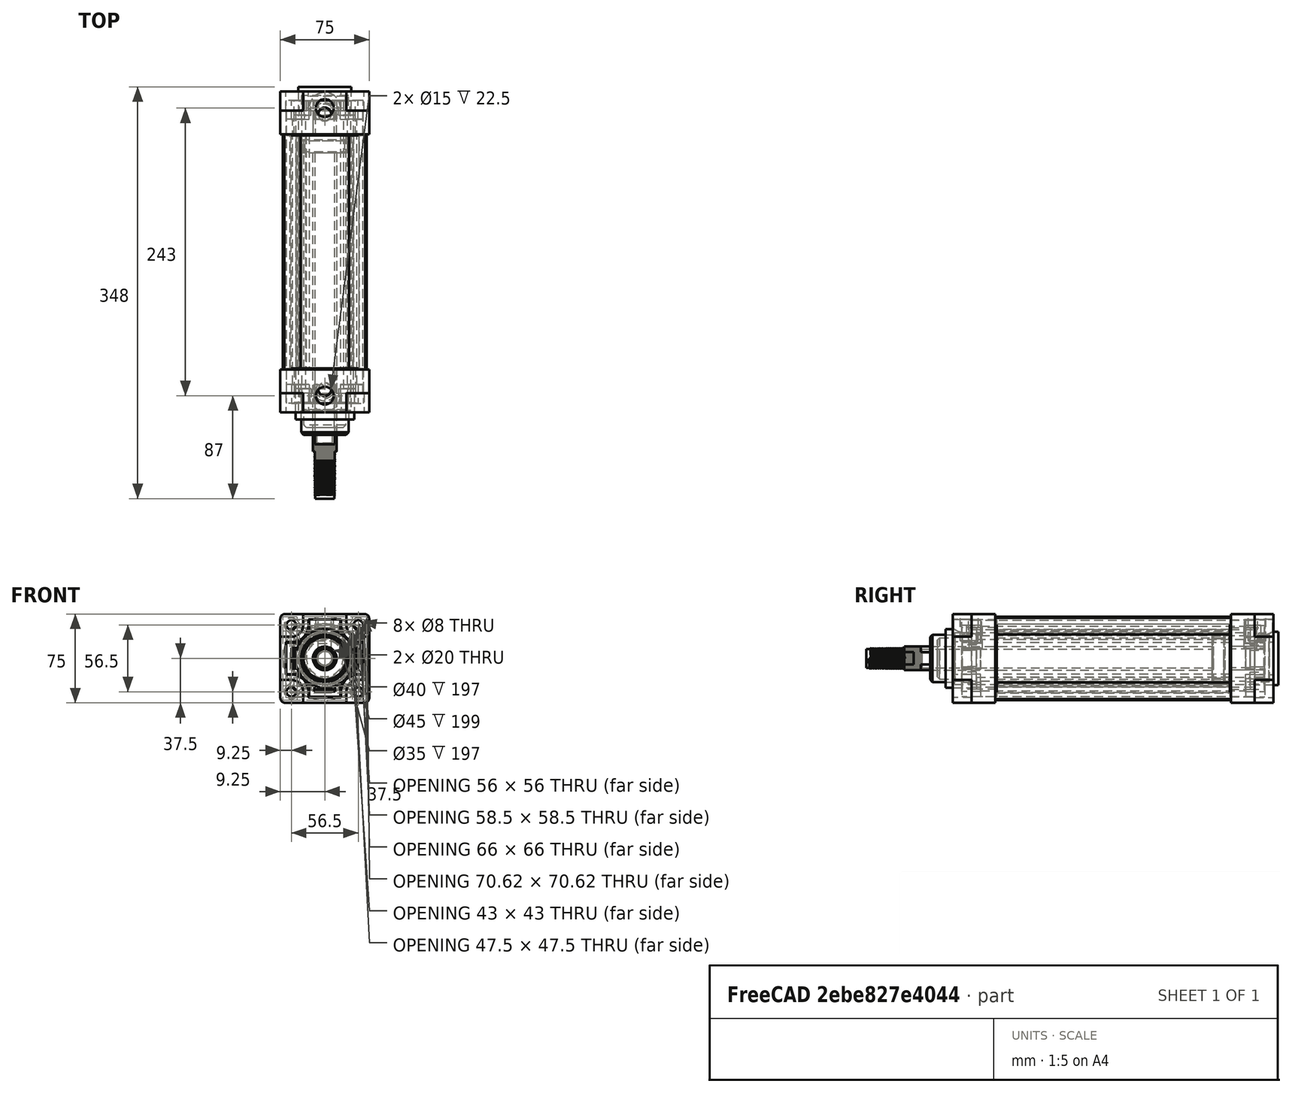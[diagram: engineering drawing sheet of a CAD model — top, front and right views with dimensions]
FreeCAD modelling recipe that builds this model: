
FCSTD DOCUMENT  (FreeCAD 0.18.4R)
Label: DA-XX-XXX-TCA show
Comment: Alejandro Alvarez\nBERSERK.DESIGN\nLicense Design Libre\n
License: Other
LicenseURL: ttps://designlibre.org/license-en/
objects: Sketcher::SketchObject×39, PartDesign::Pad×30, PartDesign::Body×9, PartDesign::Mirrored×6, PartDesign::Pocket×6, Spreadsheet::Sheet×3, PartDesign::Fillet×3, PartDesign::Chamfer×3, Part::Helix×3, PartDesign::ShapeBinder×3, PartDesign::AdditivePipe×3, Part::Fuse×3, App::Part×3, App::MeasureDistance×2
note: 147 computed .brp shape members not serialized (recipe doc carries the construction recipe); baked Part::Feature solids carry a one-line shape summary decoded from their .brp

FEATURE [Spreadsheet::Sheet] Spreadsheet  label="Medidas"
  cells = A1=Medidas Tabla; A2=CARRERRA001; B2(carrera)=150; C2=Delta Carrera; D2(delta)=5; A3=Ø; B3(diametro)=40; A4=AM; B4(am)=24; A5=B; B5(b)=35; A6=BG; B6(bg)=12; A7=EE; B7(ee)=52; A8=EEE; B8(eee)=11; C8=1/4 NPT; A9=GG; B9(gg)=29; A10=KK; B10(kk)=12; C10(kkp)=1.25; A11=KV; B11(kv)=19; A12=KW; B12(kw)=7; A13=L2; B13(l2)=21; A14=L8; B14(l8)=105; A15=MMM; B15(mmm)=16; A16=PL; B16(pl)=11.5; A17=RT; B17(rt)=6; A18=SW; B18(sw)=13; A19=TG; B19(tg)=38; A20=VA; B20(va)=4; A21=VD; B21(vd)=6; A22=VF; B22(vf)=12; A23=VG; B23(vg)=54; A24=WH; B24(wh)=30; A25=XD; B25(xd)=160; A26=AH; B26(ah)=36; A27=SA; B27(sa)=161; A28=XA; B28(xa)=163; A29=Peso Carrera 0; B29=730; A30=(gr.) Cada 10mm; B30=32; A31=Peso Total; B31==B29 + B2 / 10 * B30
FEATURE [Sketcher::SketchObject] Sketch
  MapMode = 5
  Placement = pos=(0,0,0) rot=(1,0,0;1.5708rad)
  Support = -> [XZ_Plane001]
  expr: Constraints[76] = Medidas.rt / 2 * 1.5
  expr: Constraints[72] = Medidas.tg
  expr: Constraints[74] = Medidas.tg * 0.625
  expr: Constraints[75] = Medidas.b / 2
  expr: Constraints[73] = Medidas.rt / 2
  sketch-geometry (29):
    g0: LineSegment [constr] StartX=-19 StartY=19 StartZ=0 EndX=19 EndY=19 EndZ=0
    g1: LineSegment [constr] StartX=19 StartY=19 StartZ=0 EndX=19 EndY=-19 EndZ=0
    g2: LineSegment [constr] StartX=19 StartY=-19 StartZ=0 EndX=-19 EndY=-19 EndZ=0
    g3: LineSegment [constr] StartX=-19 StartY=-19 StartZ=0 EndX=-19 EndY=19 EndZ=0
    g4: LineSegment [constr] StartX=-19 StartY=19 StartZ=0 EndX=0 EndY=0 EndZ=0
    g5: LineSegment [constr] StartX=0 StartY=0 StartZ=0 EndX=19 EndY=-19 EndZ=0
    g6: LineSegment StartX=22.182 StartY=15.818 StartZ=0 EndX=19.6716 EndY=13.3076 EndZ=0
    g7: LineSegment StartX=13.3076 StartY=19.6716 StartZ=0 EndX=15.818 EndY=22.182 EndZ=0
    g8: LineSegment [constr] StartX=0 StartY=0 StartZ=0 EndX=23.75 EndY=0 EndZ=0
    g9: ArcOfCircle CenterX=19 CenterY=19 CenterZ=0 NormalX=0 NormalY=0 NormalZ=1 AngleXU=0 Radius=4.5 StartAngle=5.49779 EndAngle=8.63938
    g10: ArcOfCircle CenterX=0 CenterY=0 CenterZ=0 NormalX=0 NormalY=0 NormalZ=1 AngleXU=0 Radius=23.75 StartAngle=0.976024 EndAngle=2.16557
    g11: LineSegment StartX=22.182 StartY=-15.818 StartZ=0 EndX=19.6716 EndY=-13.3076 EndZ=0
    g12: ArcOfCircle CenterX=19 CenterY=-19 CenterZ=0 NormalX=0 NormalY=0 NormalZ=1 AngleXU=0 Radius=4.5 StartAngle=3.92699 EndAngle=7.06858
    g13: LineSegment StartX=13.3076 StartY=-19.6716 StartZ=0 EndX=15.818 EndY=-22.182 EndZ=0
    g14: LineSegment [constr] StartX=0 StartY=0 StartZ=0 EndX=0 EndY=23.75 EndZ=0
    g15: LineSegment StartX=-22.182 StartY=15.818 StartZ=0 EndX=-19.6716 EndY=13.3076 EndZ=0
    g16: ArcOfCircle CenterX=-19 CenterY=19 CenterZ=0 NormalX=0 NormalY=0 NormalZ=1 AngleXU=0 Radius=4.5 StartAngle=0.785398 EndAngle=3.92699
    g17: LineSegment StartX=-13.3076 StartY=19.6716 StartZ=0 EndX=-15.818 EndY=22.182 EndZ=0
    g18: LineSegment StartX=-22.182 StartY=-15.818 StartZ=0 EndX=-19.6716 EndY=-13.3076 EndZ=0
    g19: ArcOfCircle CenterX=-19 CenterY=-19 CenterZ=0 NormalX=0 NormalY=0 NormalZ=1 AngleXU=0 Radius=4.5 StartAngle=2.35619 EndAngle=5.49779
    g20: LineSegment StartX=-13.3076 StartY=-19.6716 StartZ=0 EndX=-15.818 EndY=-22.182 EndZ=0
    g21: ArcOfCircle CenterX=0 CenterY=0 CenterZ=0 NormalX=0 NormalY=0 NormalZ=1 AngleXU=0 Radius=23.75 StartAngle=2.54682 EndAngle=3.73636
    g22: ArcOfCircle CenterX=0 CenterY=0 CenterZ=0 NormalX=0 NormalY=0 NormalZ=1 AngleXU=0 Radius=23.75 StartAngle=4.11762 EndAngle=5.30716
    g23: ArcOfCircle CenterX=0 CenterY=0 CenterZ=0 NormalX=0 NormalY=0 NormalZ=1 AngleXU=0 Radius=23.75 StartAngle=5.68841 EndAngle=6.87796
    g24: Circle CenterX=0 CenterY=0 CenterZ=0 NormalX=0 NormalY=0 NormalZ=1 AngleXU=0 Radius=17.5
    g25: Circle CenterX=19 CenterY=19 CenterZ=0 NormalX=0 NormalY=0 NormalZ=1 AngleXU=0 Radius=3
    g26: Circle CenterX=-19 CenterY=19 CenterZ=0 NormalX=0 NormalY=0 NormalZ=1 AngleXU=0 Radius=3
    g27: Circle CenterX=-19 CenterY=-19 CenterZ=0 NormalX=0 NormalY=0 NormalZ=1 AngleXU=0 Radius=3
    g28: Circle CenterX=19 CenterY=-19 CenterZ=0 NormalX=0 NormalY=0 NormalZ=1 AngleXU=0 Radius=3
  constraints (78):
    c: Coincident(g0,g1)
    c: Coincident(g1,g2)
    c: Coincident(g2,g3)
    c: Coincident(g3,g0)
    c: Horizontal(g0)
    c: Horizontal(g2)
    c: Vertical(g1)
    c: Vertical(g3)
    c: Coincident(g0,g4)
    c: Coincident(g4,g-1)
    c: Coincident(g4,g5)
    c: Coincident(g5,g1)
    c: Equal(g5,g4)
    c: Parallel(g5,g4)
    c: Equal(g3,g0)
    c: Parallel(g6,g7)
    c: Coincident(g-1,g8)
    c: Horizontal(g8)
    c: Angle(g8,g6) = 0.785398
    c: Coincident(g9,g0)
    c: Coincident(g9,g6)
    c: Coincident(g10,g-1)
    c: Parallel(g11,g13)
    c: Tangent(g12,g13) = -1.5708
    c: Tangent(g12,g11) = -1.5708
    c: PointOnObject(g11,g10)
    c: PointOnObject(g13,g10)
    c: Perpendicular(g6,g11)
    c: Coincident(g12,g1)
    c: Equal(g11,g6)
    c: Tangent(g9,g7) = 1.5708
    c: Equal(g9,g12)
    c: Coincident(g-1,g14)
    c: Vertical(g14)
    c: PointOnObject(g14,g10)
    c: Parallel(g15,g17)
    c: Parallel(g18,g20)
    c: Tangent(g19,g20) = 1.5708
    c: Tangent(g19,g18) = 1.5708
    c: Perpendicular(g15,g18)
    c: Equal(g18,g15)
    c: Tangent(g16,g17) = -1.5708
    c: Equal(g16,g19)
    c: Perpendicular(g7,g17)
    c: Equal(g12,g19)
    c: Coincident(g19,g2)
    c: Coincident(g0,g16)
    c: PointOnObject(g20,g10)
    c: Tangent(g16,g15) = -1.5708
    c: PointOnObject(g15,g10)
    c: Coincident(g10,g7)
    c: Coincident(g23,g6)
    c: Equal(g10,g21)
    c: Coincident(g10,g17)
    c: Coincident(g10,g21)
    c: Equal(g21,g22)
    c: PointOnObject(g21,g18)
    c: PointOnObject(g22,g20)
    c: Coincident(g21,g22)
    c: Equal(g22,g23)
    c: PointOnObject(g23,g11)
    c: Coincident(g22,g23)
    c: PointOnObject(g22,g13)
    c: PointOnObject(g21,g15)
    c: Coincident(g24,g-1)
    c: Coincident(g25,g0)
    c: Coincident(g26,g0)
    c: Coincident(g27,g2)
    c: Coincident(g28,g1)
    c: Equal(g28,g25)
    c: Equal(g25,g26)
    c: Equal(g26,g27)
    c: DistanceX(g0,g0) = 38
    c: Radius(g28) = 3
    c: Radius(g23) = 23.75
    c: Radius(g24) = 17.5
    c: Radius(g12) = 4.5
    c: PointOnObject(g8,g23)
FEATURE [PartDesign::Pad] Pad
  Length = 197
  Length2 = 100
  Midplane = true
  Placement = pos=(0,0,0) rot=(1,0,0;1.5708rad)
  Profile = -> Sketch
  Refine = true
  Type = 0
  expr: Length = Medidas.l8 + Medidas.carrera - 2 * Medidas.gg
FEATURE [Sketcher::SketchObject] Sketch001
  ExternalGeometry = -> [Pad]
  MapMode = 5
  Placement = pos=(0,-98.5,-1.01921e-11) rot=(1,0,0;1.5708rad)
  Support = -> [Pad]
  expr: Constraints[37] = Medidas.mmm / 2
  expr: Constraints[15] = Medidas.ee
  expr: Constraints[33] = Medidas.tg
  expr: Constraints[32] = Medidas.rt / 2
  sketch-geometry (15):
    g0: LineSegment StartX=-26 StartY=26 StartZ=0 EndX=26 EndY=26 EndZ=0
    g1: LineSegment StartX=26 StartY=26 StartZ=0 EndX=26 EndY=-26 EndZ=0
    g2: LineSegment StartX=26 StartY=-26 StartZ=0 EndX=-26 EndY=-26 EndZ=0
    g3: LineSegment StartX=-26 StartY=-26 StartZ=0 EndX=-26 EndY=26 EndZ=0
    g4: LineSegment [constr] StartX=-26 StartY=26 StartZ=0 EndX=0 EndY=0 EndZ=0
    g5: LineSegment [constr] StartX=0 StartY=0 StartZ=0 EndX=26 EndY=-26 EndZ=0
    g6: Circle CenterX=-19 CenterY=19 CenterZ=0 NormalX=0 NormalY=0 NormalZ=1 AngleXU=0 Radius=3
    g7: Circle CenterX=19 CenterY=19 CenterZ=0 NormalX=0 NormalY=0 NormalZ=1 AngleXU=0 Radius=3
    g8: Circle CenterX=19 CenterY=-19 CenterZ=0 NormalX=0 NormalY=0 NormalZ=1 AngleXU=0 Radius=3
    g9: Circle CenterX=-19 CenterY=-19 CenterZ=0 NormalX=0 NormalY=0 NormalZ=1 AngleXU=0 Radius=3
    g10: LineSegment [constr] StartX=-19 StartY=19 StartZ=0 EndX=19 EndY=19 EndZ=0
    g11: LineSegment [constr] StartX=19 StartY=19 StartZ=0 EndX=19 EndY=-19 EndZ=0
    g12: LineSegment [constr] StartX=19 StartY=-19 StartZ=0 EndX=-19 EndY=-19 EndZ=0
    g13: LineSegment [constr] StartX=-19 StartY=-19 StartZ=0 EndX=-19 EndY=19 EndZ=0
    g14: Circle CenterX=0 CenterY=0 CenterZ=0 NormalX=0 NormalY=0 NormalZ=1 AngleXU=0 Radius=8
  constraints (38):
    c: Coincident(g0,g1)
    c: Coincident(g1,g2)
    c: Coincident(g2,g3)
    c: Coincident(g3,g0)
    c: Horizontal(g0)
    c: Horizontal(g2)
    c: Vertical(g1)
    c: Vertical(g3)
    c: Coincident(g0,g4)
    c: Coincident(g4,g-1)
    c: Coincident(g4,g5)
    c: Coincident(g5,g1)
    c: Parallel(g5,g4)
    c: Equal(g5,g4)
    c: Equal(g0,g3)
    c: DistanceX(g2,g2) = 52
    c: PointOnObject(g6,g4)
    c: Coincident(g10,g11)
    c: Coincident(g11,g12)
    c: Coincident(g12,g13)
    c: Coincident(g13,g10)
    c: Horizontal(g10)
    c: Horizontal(g12)
    c: Vertical(g11)
    c: Vertical(g13)
    c: Coincident(g10,g6)
    c: Coincident(g11,g8)
    c: Coincident(g7,g10)
    c: Coincident(g12,g9)
    c: Equal(g9,g8)
    c: Equal(g8,g7)
    c: Equal(g7,g6)
    c: Radius(g6) = 3
    c: DistanceX(g10,g10) = 38
    c: Equal(g13,g10)
    c: Symmetric(g7,g6,g-2)
    c: Coincident(g14,g-1)
    c: Radius(g14) = 8
FEATURE [PartDesign::Pad] Pad001
  BaseFeature = -> Pad
  Length = 17
  Length2 = 100
  Placement = pos=(0,0,0) rot=(1,0,0;1.5708rad)
  Profile = -> Sketch001
  Refine = true
  Type = 0
  expr: Length = Medidas.gg - Medidas.bg
FEATURE [Sketcher::SketchObject] Sketch002
  ExternalGeometry = -> [Pad001]
  MapMode = 5
  Placement = pos=(0,-115.5,-1.19311e-11) rot=(1,0,0;1.5708rad)
  Support = -> [Pad001]
  expr: Constraints[114] = Medidas.rt * 1.25 + 4.5
  expr: Constraints[45] = Medidas.tg - 2.5 * Medidas.rt
  expr: Constraints[48] = Medidas.rt * 1.25
  sketch-geometry (37):
    g0: LineSegment StartX=-26 StartY=11.5 StartZ=0 EndX=-26 EndY=-11.5 EndZ=0
    g1: LineSegment StartX=-26 StartY=-11.5 StartZ=0 EndX=-19 EndY=-11.5 EndZ=0
    g2: LineSegment StartX=-11.5 StartY=-19 StartZ=0 EndX=-11.5 EndY=-26 EndZ=0
    g3: LineSegment StartX=-11.5 StartY=-26 StartZ=0 EndX=11.5 EndY=-26 EndZ=0
    g4: LineSegment StartX=11.5 StartY=-26 StartZ=0 EndX=11.5 EndY=-19 EndZ=0
    g5: LineSegment StartX=19 StartY=-11.5 StartZ=0 EndX=26 EndY=-11.5 EndZ=0
    g6: LineSegment StartX=26 StartY=-11.5 StartZ=0 EndX=26 EndY=11.5 EndZ=0
    g7: LineSegment StartX=26 StartY=11.5 StartZ=0 EndX=19 EndY=11.5 EndZ=0
    g8: LineSegment StartX=11.5 StartY=19 StartZ=0 EndX=11.5 EndY=26 EndZ=0
    g9: LineSegment StartX=11.5 StartY=26 StartZ=0 EndX=-11.5 EndY=26 EndZ=0
    g10: LineSegment StartX=-11.5 StartY=26 StartZ=0 EndX=-11.5 EndY=19 EndZ=0
    g11: LineSegment StartX=-19 StartY=11.5 StartZ=0 EndX=-26 EndY=11.5 EndZ=0
    g12: ArcOfCircle CenterX=-19 CenterY=19 CenterZ=0 NormalX=0 NormalY=0 NormalZ=1 AngleXU=0 Radius=7.5 StartAngle=4.71239 EndAngle=6.28319
    g13: ArcOfCircle CenterX=-19 CenterY=-19 CenterZ=0 NormalX=0 NormalY=0 NormalZ=1 AngleXU=0 Radius=7.5 StartAngle=0 EndAngle=1.5708
    g14: ArcOfCircle CenterX=19 CenterY=-19 CenterZ=0 NormalX=0 NormalY=0 NormalZ=1 AngleXU=0 Radius=7.5 StartAngle=1.5708 EndAngle=3.14159
    g15: ArcOfCircle CenterX=19 CenterY=19 CenterZ=0 NormalX=0 NormalY=0 NormalZ=1 AngleXU=0 Radius=7.5 StartAngle=3.14159 EndAngle=4.71239
    g16: LineSegment StartX=-7 StartY=21.5 StartZ=0 EndX=-7 EndY=19 EndZ=0
    g17: LineSegment StartX=-19 StartY=7 StartZ=0 EndX=-21.5 EndY=7 EndZ=0
    g18: LineSegment StartX=-21.5 StartY=7 StartZ=0 EndX=-21.5 EndY=-7 EndZ=0
    g19: LineSegment StartX=-21.5 StartY=-7 StartZ=0 EndX=-19 EndY=-7 EndZ=0
    g20: LineSegment StartX=-7 StartY=-19 StartZ=0 EndX=-7 EndY=-21.5 EndZ=0
    g21: LineSegment StartX=-7 StartY=-21.5 StartZ=0 EndX=7 EndY=-21.5 EndZ=0
    g22: LineSegment StartX=7 StartY=-21.5 StartZ=0 EndX=7 EndY=-19 EndZ=0
    g23: LineSegment StartX=19 StartY=-7 StartZ=0 EndX=21.5 EndY=-7 EndZ=0
    g24: LineSegment StartX=21.5 StartY=-7 StartZ=0 EndX=21.5 EndY=7 EndZ=0
    g25: LineSegment StartX=21.5 StartY=7 StartZ=0 EndX=19 EndY=7 EndZ=0
    g26: LineSegment StartX=7 StartY=19 StartZ=0 EndX=7 EndY=21.5 EndZ=0
    g27: LineSegment StartX=7 StartY=21.5 StartZ=0 EndX=-7 EndY=21.5 EndZ=0
    g28: LineSegment [constr] StartX=-21.5 StartY=-7 StartZ=0 EndX=-26 EndY=-7 EndZ=0
    g29: LineSegment [constr] StartX=21.5 StartY=-7 StartZ=0 EndX=26 EndY=-7 EndZ=0
    g30: LineSegment [constr] StartX=-7 StartY=21.5 StartZ=0 EndX=-7 EndY=26 EndZ=0
    g31: LineSegment [constr] StartX=-7 StartY=-21.5 StartZ=0 EndX=-7 EndY=-26 EndZ=0
    g32: LineSegment [constr] StartX=-21.5 StartY=-7 StartZ=0 EndX=-21.5 EndY=-11.5 EndZ=0
    g33: ArcOfCircle CenterX=-19 CenterY=19 CenterZ=0 NormalX=0 NormalY=0 NormalZ=1 AngleXU=0 Radius=12 StartAngle=4.71239 EndAngle=6.28319
    g34: ArcOfCircle CenterX=19 CenterY=19 CenterZ=0 NormalX=0 NormalY=0 NormalZ=1 AngleXU=0 Radius=12 StartAngle=3.14159 EndAngle=4.71239
    g35: ArcOfCircle CenterX=19 CenterY=-19 CenterZ=0 NormalX=0 NormalY=0 NormalZ=1 AngleXU=0 Radius=12 StartAngle=1.5708 EndAngle=3.14159
    g36: ArcOfCircle CenterX=-19 CenterY=-19 CenterZ=0 NormalX=0 NormalY=0 NormalZ=1 AngleXU=0 Radius=12 StartAngle=0 EndAngle=1.5708
  constraints (115):
    c: Coincident(g1,g0)
    c: Horizontal(g1)
    c: Vertical(g2)
    c: Coincident(g2,g3)
    c: Coincident(g3,g4)
    c: Vertical(g4)
    c: Horizontal(g5)
    c: Coincident(g5,g6)
    c: Coincident(g6,g7)
    c: Vertical(g8)
    c: Coincident(g8,g9)
    c: Horizontal(g9)
    c: Coincident(g9,g10)
    c: Coincident(g11,g0)
    c: Horizontal(g11)
    c: PointOnObject(g0,g-3)
    c: Symmetric(g0,g0,g-1)
    c: Symmetric(g6,g5,g-1)
    c: Symmetric(g8,g9,g-2)
    c: PointOnObject(g9,g-4)
    c: Vertical(g10)
    c: Horizontal(g7)
    c: Symmetric(g3,g2,g-2)
    c: PointOnObject(g3,g-6)
    c: Equal(g10,g8)
    c: Equal(g8,g7)
    c: Equal(g7,g5)
    c: Equal(g5,g4)
    c: Equal(g4,g2)
    c: Equal(g2,g1)
    c: Equal(g1,g11)
    c: Equal(g3,g0)
    c: Equal(g0,g9)
    c: Equal(g9,g6)
    c: Coincident(g12,g10)
    c: Coincident(g12,g11)
    c: Coincident(g13,g1)
    c: Coincident(g13,g2)
    c: Coincident(g14,g4)
    c: Coincident(g14,g5)
    c: Coincident(g15,g7)
    c: Coincident(g15,g8)
    c: Equal(g15,g12)
    c: Equal(g12,g13)
    c: Equal(g13,g14)
    c: DistanceX(g3,g3) = 23
    c: Vertical(g1,g13)
    c: PointOnObject(g6,g-5)
    c: Radius(g13) = 7.5
    c: Vertical(g16)
    c: Coincident(g17,g18)
    c: Vertical(g18)
    c: Coincident(g18,g19)
    c: Horizontal(g19)
    c: Vertical(g20)
    c: Coincident(g20,g21)
    c: Horizontal(g21)
    c: Coincident(g21,g22)
    c: Vertical(g22)
    c: Horizontal(g23)
    c: Coincident(g23,g24)
    c: Vertical(g24)
    c: Coincident(g24,g25)
    c: Horizontal(g25)
    c: Vertical(g26)
    c: Coincident(g26,g27)
    c: Coincident(g27,g16)
    c: Horizontal(g27)
    c: Symmetric(g26,g16,g-2)
    c: Symmetric(g17,g18,g-1)
    c: Symmetric(g20,g21,g-2)
    c: Symmetric(g23,g24,g-1)
    c: Equal(g24,g27)
    c: Equal(g27,g18)
    c: Equal(g18,g21)
    c: Equal(g20,g22)
    c: Equal(g22,g23)
    c: Equal(g23,g25)
    c: Equal(g25,g26)
    c: Equal(g26,g16)
    c: Equal(g16,g17)
    c: Equal(g17,g19)
    c: Horizontal(g17)
    c: Coincident(g18,g28)
    c: PointOnObject(g28,g0)
    c: Horizontal(g28)
    c: Coincident(g23,g29)
    c: PointOnObject(g29,g6)
    c: Horizontal(g29)
    c: Coincident(g16,g30)
    c: PointOnObject(g30,g9)
    c: Vertical(g30)
    c: Coincident(g20,g31)
    c: Vertical(g31)
    c: Equal(g29,g31)
    c: Equal(g31,g28)
    c: Equal(g28,g30)
    c: DistanceX(g28,g28) = 4.5
    c: Vertical(g32)
    c: PointOnObject(g32,g1)
    c: Coincident(g18,g32)
    c: Equal(g32,g28)
    c: PointOnObject(g31,g3)
    c: Coincident(g33,g16)
    c: Coincident(g33,g17)
    c: Coincident(g34,g25)
    c: Coincident(g34,g26)
    c: Coincident(g35,g22)
    c: Coincident(g35,g23)
    c: Tangent(g36,g19) = 1.5708
    c: Tangent(g36,g20) = 1.5708
    c: Vertical(g35,g23)
    c: Equal(g33,g34)
    c: Equal(g34,g35)
    c: Radius(g35) = 12
FEATURE [PartDesign::Pad] Pad002
  BaseFeature = -> Pad001
  Length = 12
  Length2 = 100
  Placement = pos=(0,0,0) rot=(1,0,0;1.5708rad)
  Profile = -> Sketch002
  Refine = true
  Type = 0
  expr: Length = Medidas.bg
FEATURE [Sketcher::SketchObject] Sketch003
  MapMode = 5
  Placement = pos=(0,-127.5,-1.31123e-11) rot=(1,0,0;1.5708rad)
  Support = -> [Pad002]
  expr: Constraints[3] = Medidas.b / 2 * 1.1
  expr: Constraints[2] = Medidas.mmm / 2
  sketch-geometry (2):
    g0: Circle CenterX=0 CenterY=0 CenterZ=0 NormalX=0 NormalY=0 NormalZ=1 AngleXU=0 Radius=8
    g1: Circle CenterX=0 CenterY=0 CenterZ=0 NormalX=0 NormalY=0 NormalZ=1 AngleXU=0 Radius=19.25
  constraints (4):
    c: Coincident(g0,g-1)
    c: Coincident(g1,g-1)
    c: Radius(g0) = 8
    c: Radius(g1) = 19.25
FEATURE [PartDesign::Pad] Pad003
  BaseFeature = -> Pad002
  Length = 18
  Length2 = 100
  Placement = pos=(0,0,0) rot=(1,0,0;1.5708rad)
  Profile = -> Sketch003
  Refine = true
  Type = 0
  expr: Length = Medidas.bg + Medidas.vd
FEATURE [Sketcher::SketchObject] Sketch004
  MapMode = 5
  Placement = pos=(0,-133.5,-1.37692e-11) rot=(1,0,0;1.5708rad)
  Support = -> [Pad003]
  expr: Constraints[3] = Medidas.mmm / 2
  expr: Constraints[2] = Medidas.b / 2
  sketch-geometry (2):
    g0: Circle CenterX=0 CenterY=0 CenterZ=0 NormalX=0 NormalY=0 NormalZ=1 AngleXU=0 Radius=17.5
    g1: Circle CenterX=0 CenterY=0 CenterZ=0 NormalX=0 NormalY=0 NormalZ=1 AngleXU=0 Radius=8
  constraints (4):
    c: Coincident(g0,g-1)
    c: Coincident(g1,g-1)
    c: Radius(g0) = 17.5
    c: Radius(g1) = 8
FEATURE [PartDesign::Pad] Pad004
  BaseFeature = -> Pad003
  Length = 15
  Length2 = 100
  Placement = pos=(0,0,0) rot=(1,0,0;1.5708rad)
  Profile = -> Sketch004
  Refine = true
  Type = 0
  expr: Length = Medidas.l2 - Medidas.vd
FEATURE [PartDesign::Mirrored] Mirrored
  BaseFeature = -> Pad004
  MirrorPlane = -> XZ_Plane001
  Originals = -> [Pad001]
  Placement = pos=(0,0,0) rot=(1,0,0;1.5708rad)
  Refine = true
FEATURE [PartDesign::Mirrored] Mirrored001
  BaseFeature = -> Mirrored
  MirrorPlane = -> XZ_Plane001
  Originals = -> [Pad002]
  Placement = pos=(0,0,0) rot=(1,0,0;1.5708rad)
  Refine = true
FEATURE [Sketcher::SketchObject] Sketch005
  MapMode = 5
  Placement = pos=(0,-2.7093e-12,26) rot=(0,0,1;3.14159rad)
  Support = -> [Mirrored001]
  expr: Constraints[1] = Medidas.b / 2
  sketch-geometry (1):
    g0: Circle CenterX=0 CenterY=0 CenterZ=0 NormalX=0 NormalY=0 NormalZ=1 AngleXU=0 Radius=17.5
  constraints (2):
    c: Coincident(g0,g-1)
    c: Radius(g0) = 17.5
FEATURE [PartDesign::Pad] Pad005
  BaseFeature = -> Mirrored001
  Length = 16
  Length2 = 100
  Placement = pos=(0,0,0) rot=(1,0,0;1.5708rad)
  Profile = -> Sketch005
  Refine = true
  Type = 0
  expr: Length = Medidas.bg + Medidas.va
FEATURE [PartDesign::Fillet] Fillet
  Base = -> Pad005 [Edge27,Edge21,Edge39,Edge213,Edge201,Edge200,Edge28,Edge207]
  BaseFeature = -> Pad005
  Placement = pos=(0,0,0) rot=(1,0,0;1.5708rad)
  Radius = 3
  expr: Radius = Medidas.rt / 2
FEATURE [PartDesign::Chamfer] Chamfer
  Base = -> Fillet [Edge306]
  BaseFeature = -> Fillet
  Placement = pos=(0,0,0) rot=(1,0,0;1.5708rad)
  Size = 2
FEATURE [Sketcher::SketchObject] Sketch006
  ExternalGeometry = -> [Chamfer]
  MapMode = 5
  Placement = pos=(0,-2.6713e-12,26) rot=(0,0,1;3.14159rad)
  Support = -> [Chamfer]
  expr: Constraints[5] = Medidas.pl
  expr: Constraints[4] = Medidas.pl
  expr: Constraints[3] = Medidas.eee / 2
  sketch-geometry (2):
    g0: Circle CenterX=0 CenterY=116 CenterZ=0 NormalX=0 NormalY=0 NormalZ=1 AngleXU=0 Radius=5.5
    g1: Circle CenterX=0 CenterY=-116 CenterZ=0 NormalX=0 NormalY=0 NormalZ=1 AngleXU=0 Radius=5.5
  constraints (6):
    c: PointOnObject(g0,g-2)
    c: PointOnObject(g1,g-2)
    c: Equal(g1,g0)
    c: Radius(g0) = 5.5
    c: DistanceY(g0,g-4) = 11.5
    c: DistanceY(g-3,g1) = 11.5
FEATURE [PartDesign::Pocket] Pocket
  BaseFeature = -> Chamfer
  Length = 17.5
  Length2 = 100
  Placement = pos=(0,0,0) rot=(1,0,0;1.5708rad)
  Profile = -> Sketch006
  Refine = true
  Type = 0
  expr: Length = Medidas.b / 2
FEATURE [Sketcher::SketchObject] Sketch007
  ExternalGeometry = -> [Pocket]
  MapMode = 5
  Placement = pos=(0,-2.7093e-12,26) rot=(0,0,1;3.14159rad)
  Support = -> [Pocket]
  expr: Constraints[6] = Medidas.eee * 0.9
  sketch-geometry (4):
    g0: Circle CenterX=0 CenterY=116 CenterZ=0 NormalX=0 NormalY=0 NormalZ=1 AngleXU=0 Radius=5.5
    g1: Circle CenterX=0 CenterY=116 CenterZ=0 NormalX=0 NormalY=0 NormalZ=1 AngleXU=0 Radius=9.9
    g2: Circle CenterX=0 CenterY=-116 CenterZ=0 NormalX=0 NormalY=0 NormalZ=1 AngleXU=0 Radius=5.5
    g3: Circle CenterX=0 CenterY=-116 CenterZ=0 NormalX=0 NormalY=0 NormalZ=1 AngleXU=0 Radius=9.9
  constraints (8):
    c: Coincident(g0,g-4)
    c: Coincident(g1,g0)
    c: Coincident(g2,g-3)
    c: Coincident(g3,g2)
    c: Equal(g2,g0)
    c: Equal(g1,g3)
    c: Radius(g3) = 9.9
    c: Equal(g2,g-3)
FEATURE [PartDesign::Pad] Pad006
  BaseFeature = -> Pocket
  Length = 17.5
  Length2 = 100
  Placement = pos=(0,0,0) rot=(1,0,0;1.5708rad)
  Profile = -> Sketch007
  Refine = true
  Reversed = true
  Type = 0
  expr: Length = Medidas.b / 2
FEATURE [PartDesign::Body] Body  label="Barrel+Endcap"
  Group = -> [Sketch,Pad,Sketch001,Pad001,Sketch002,Pad002,Sketch003,Pad003,Sketch004,Pad004,Mirrored,Mirrored001,Sketch005,Pad005,Fillet,Chamfer,Sketch006,Pocket,Sketch007,Pad006]
  Origin = -> Origin001
  Tip = -> Pad006
FEATURE [Sketcher::SketchObject] Sketch008
  MapMode = 5
  Placement = pos=(0,0,0) rot=(1,0,0;1.5708rad)
  Support = -> [XZ_Plane002]
  expr: Constraints[1] = Medidas.b / 2 * 0.95
  sketch-geometry (1):
    g0: Circle CenterX=0 CenterY=0 CenterZ=0 NormalX=0 NormalY=0 NormalZ=1 AngleXU=0 Radius=16.625
  constraints (2):
    c: Coincident(g0,g-1)
    c: Radius(g0) = 16.625
FEATURE [PartDesign::Pad] Pad007
  Length = 10
  Length2 = 100
  Placement = pos=(0,0,0) rot=(1,0,0;1.5708rad)
  Profile = -> Sketch008
  Refine = true
  Type = 0
FEATURE [Sketcher::SketchObject] Sketch009
  MapMode = 5
  Placement = pos=(0,0,0) rot=(-1,0,0;1.5708rad)
  Support = -> [Pad007]
  expr: Constraints[1] = Medidas.mmm / 2
  sketch-geometry (1):
    g0: Circle CenterX=0 CenterY=0 CenterZ=0 NormalX=0 NormalY=0 NormalZ=1 AngleXU=0 Radius=8
  constraints (2):
    c: Coincident(g0,g-1)
    c: Radius(g0) = 8
FEATURE [PartDesign::Pad] Pad008
  BaseFeature = -> Pad007
  Length = 255
  Length2 = 100
  Placement = pos=(0,0,0) rot=(1,0,0;1.5708rad)
  Profile = -> Sketch009
  Refine = true
  Reversed = true
  Type = 0
  expr: Length = Medidas.l8 + Medidas.carrera
FEATURE [Sketcher::SketchObject] Sketch010
  MapMode = 5
  Placement = pos=(0,-255,-2.63856e-11) rot=(1,0,0;1.5708rad)
  Support = -> [Pad008]
  expr: Constraints[22] = Medidas.sw
  expr: Constraints[19] = Medidas.sw
  sketch-geometry (8):
    g0: LineSegment StartX=-19.5 StartY=6.5 StartZ=0 EndX=-6.5 EndY=6.5 EndZ=0
    g1: LineSegment StartX=-6.5 StartY=6.5 StartZ=0 EndX=-6.5 EndY=-6.5 EndZ=0
    g2: LineSegment StartX=-6.5 StartY=-6.5 StartZ=0 EndX=-19.5 EndY=-6.5 EndZ=0
    g3: LineSegment StartX=-19.5 StartY=-6.5 StartZ=0 EndX=-19.5 EndY=6.5 EndZ=0
    g4: LineSegment StartX=19.5 StartY=6.5 StartZ=0 EndX=6.5 EndY=6.5 EndZ=0
    g5: LineSegment StartX=6.5 StartY=6.5 StartZ=0 EndX=6.5 EndY=-6.5 EndZ=0
    g6: LineSegment StartX=6.5 StartY=-6.5 StartZ=0 EndX=19.5 EndY=-6.5 EndZ=0
    g7: LineSegment StartX=19.5 StartY=-6.5 StartZ=0 EndX=19.5 EndY=6.5 EndZ=0
  constraints (23):
    c: Coincident(g0,g1)
    c: Coincident(g1,g2)
    c: Coincident(g2,g3)
    c: Coincident(g3,g0)
    c: Horizontal(g0)
    c: Horizontal(g2)
    c: Vertical(g1)
    c: Vertical(g3)
    c: Coincident(g4,g5)
    c: Coincident(g5,g6)
    c: Coincident(g6,g7)
    c: Coincident(g7,g4)
    c: Horizontal(g4)
    c: Horizontal(g6)
    c: Vertical(g5)
    c: Vertical(g7)
    c: Symmetric(g0,g4,g-2)
    c: Equal(g5,g1)
    c: Equal(g6,g2)
    c: DistanceX(g0,g4) = 13
    c: Symmetric(g0,g2,g-1)
    c: Equal(g0,g3)
    c: DistanceX(g0,g0) = 13
FEATURE [PartDesign::Pocket] Pocket001
  BaseFeature = -> Pad008
  Length = 7
  Length2 = 100
  Placement = pos=(0,0,0) rot=(1,0,0;1.5708rad)
  Profile = -> Sketch010
  Refine = true
  Type = 0
  expr: Length = Medidas.kw
FEATURE [Sketcher::SketchObject] Sketch011
  MapMode = 5
  Placement = pos=(0,-255,-2.63856e-11) rot=(1,0,0;1.5708rad)
  Support = -> [Pocket001]
  expr: Constraints[1] = Medidas.kk / 2
  sketch-geometry (1):
    g0: Circle CenterX=0 CenterY=0 CenterZ=0 NormalX=0 NormalY=0 NormalZ=1 AngleXU=0 Radius=6
  constraints (2):
    c: Coincident(g0,g-1)
    c: Radius(g0) = 6
FEATURE [Part::Helix] Helix  label="Thread Helice"
  Angle = 0
  AttacherType = Attacher::AttachEngine3D
  Height = 24
  LocalCoord = 0
  Pitch = 1.25
  Placement = pos=(0,0,0) rot=(-1,0,0;1.5708rad)
  Radius = 6
  Style = 1
  expr: Radius = Medidas.kk / 2
  expr: Height = Medidas.am
  expr: Pitch = Medidas.kkp
FEATURE [Sketcher::SketchObject] Sketch012
  MapMode = 5
  Support = -> [XY_Plane003]
  expr: Constraints[6] = Medidas.kk / 2 * 0.96
  sketch-geometry (3):
    g0: LineSegment StartX=5.76 StartY=0.4 StartZ=0 EndX=5.76 EndY=-0.4 EndZ=0
    g1: LineSegment StartX=5.76 StartY=-0.4 StartZ=0 EndX=6.76 EndY=0 EndZ=0
    g2: LineSegment StartX=6.76 StartY=0 StartZ=0 EndX=5.76 EndY=0.4 EndZ=0
  constraints (9):
    c: Vertical(g0)
    c: Coincident(g0,g1)
    c: PointOnObject(g1,g-1)
    c: Coincident(g1,g2)
    c: Coincident(g2,g0)
    c: Symmetric(g0,g0,g-1)
    c: DistanceX(g-1,g0) = 5.76
    c: DistanceX(g0,g1) = 1
    c: DistanceY(g0,g0) = 0.8
FEATURE [PartDesign::ShapeBinder] ReferenceHelix001  label="ReferenceHelix"
  Placement = pos=(0,0,0) rot=(-1,0,0;1.5708rad)
  Support = -> [Helix]
  TraceSupport = false
FEATURE [PartDesign::AdditivePipe] AdditivePipe
  AuxilleryCurvelinear = true
  AuxillerySpineTangent = false
  Binormal = (0,0,0)
  Mode = 2
  Profile = -> Sketch012
  Refine = true
  Spine = -> ReferenceHelix001 [Edge1,Edge2,Edge3,Edge4,Edge5,Edge6,Edge7,Edge8,Edge9,Edge10,Edge11,Edge12,Edge13,Edge14,Edge15,Edge16,Edge17,Edge18,Edge19,Edge20]
  SpineTangent = false
  Transformation = 0
  Transition = 0
FEATURE [PartDesign::Body] Body002  label="Thread"
  Group = -> [Sketch012,AdditivePipe,ReferenceHelix001]
  Origin = -> Origin003
  Placement = pos=(0,-279,0) rot=(0,0,1;0rad)
  Tip = -> AdditivePipe
  expr: Placement.Base.y = -Medidas.l8 - Medidas.carrera - Medidas.l2 - 3
FEATURE [PartDesign::Pad] Pad009
  BaseFeature = -> Pocket001
  Length = 24
  Length2 = 100
  Placement = pos=(0,0,0) rot=(1,0,0;1.5708rad)
  Profile = -> Sketch011
  Refine = true
  Type = 0
  expr: Length = Medidas.am
FEATURE [PartDesign::Body] Body001  label="Piston+rod"
  Group = -> [Sketch008,Pad007,Sketch009,Pad008,Sketch010,Pocket001,Sketch011,Pad009]
  Origin = -> Origin002
  Tip = -> Pad009
FEATURE [Part::Fuse] Fusion  label="Piston Rod"
  Base = -> Body001
  Placement = pos=(0,93.5,0) rot=(0,0,1;0rad)
  Refine = true
  Tool = -> Body002
  expr: Placement.Base.y = (Medidas.l8 + Medidas.carrera) / 2 - Medidas.gg + -Medidas.delta
FEATURE [App::Part] Part
  Group = -> [Body,Body001,Helix,Body002,Fusion]
  Id = DA-XX-XXX-TCA
  License = CC BY 3.0
  LicenseURL = http://creativecommons.org/licenses/by/3.0/
  Origin = -> Origin
  Type = Pneumatic cylinder
FEATURE [Spreadsheet::Sheet] Spreadsheet001  label="Medidas001"
  cells = A1=Medidas Tabla; A2=CARRERRA001; B2(carrera)=150; C2=Delta Carrera; D2(delta)=5; A3=Ø; B3(diametro)=50; A4=AM; B4(am)=32; A5=B; B5(b)=40; A6=BG; B6(bg)=16; A7=EE; B7(ee)=65; A8=EEE; B8(eee)=11; C8=1/4 NPT; A9=GG; B9(gg)=29.5; A10=KK; B10(kk)=16; C10(kkp)=1.5; A11=KV; B11(kv)=24; A12=KW; B12(kw)=8; A13=L2; B13(l2)=26.5; A14=L8; B14(l8)=106; A15=MMM; B15(mmm)=20; A16=PL; B16(pl)=11.5; A17=RT; B17(rt)=8; A18=SW; B18(sw)=17; A19=TG; B19(tg)=46.5; A20=VA; B20(va)=4; A21=VD; B21(vd)=6; A22=VF; B22(vf)=16; A23=VG; B23(vg)=69; A24=WH; B24(wh)=37; A25=XD; B25(xd)=170; A26=AH; B26(ah)=45; A27=SA; B27(sa)=170; A28=XA; B28(xa)=175; A29=Peso Carrera 0; B29=1150; A30=(gr.) Cada 10mm; B30=175; A31=Peso Total; B31==B29 + B2 / 10 * B30
FEATURE [Sketcher::SketchObject] Sketch013
  MapMode = 5
  Placement = pos=(0,0,0) rot=(1,0,0;1.5708rad)
  Support = -> [XZ_Plane005]
  expr: Constraints[76] = Medidas.rt / 2 * 1.5
  expr: Constraints[72] = Medidas.tg
  expr: Constraints[74] = Medidas.tg * 0.625
  expr: Constraints[75] = Medidas.b / 2
  expr: Constraints[73] = Medidas.rt / 2
  sketch-geometry (29):
    g0: LineSegment [constr] StartX=-23.25 StartY=23.25 StartZ=0 EndX=23.25 EndY=23.25 EndZ=0
    g1: LineSegment [constr] StartX=23.25 StartY=23.25 StartZ=0 EndX=23.25 EndY=-23.25 EndZ=0
    g2: LineSegment [constr] StartX=23.25 StartY=-23.25 StartZ=0 EndX=-23.25 EndY=-23.25 EndZ=0
    g3: LineSegment [constr] StartX=-23.25 StartY=-23.25 StartZ=0 EndX=-23.25 EndY=23.25 EndZ=0
    g4: LineSegment [constr] StartX=-23.25 StartY=23.25 StartZ=0 EndX=0 EndY=0 EndZ=0
    g5: LineSegment [constr] StartX=0 StartY=0 StartZ=0 EndX=23.25 EndY=-23.25 EndZ=0
    g6: LineSegment StartX=27.4926 StartY=19.0074 StartZ=0 EndX=24.3502 EndY=15.8649 EndZ=0
    g7: LineSegment StartX=15.8649 StartY=24.3502 StartZ=0 EndX=19.0074 EndY=27.4926 EndZ=0
    g8: LineSegment [constr] StartX=0 StartY=0 StartZ=0 EndX=29.0625 EndY=0 EndZ=0
    g9: ArcOfCircle CenterX=23.25 CenterY=23.25 CenterZ=0 NormalX=0 NormalY=0 NormalZ=1 AngleXU=0 Radius=6 StartAngle=5.49779 EndAngle=8.63938
    g10: ArcOfCircle CenterX=0 CenterY=0 CenterZ=0 NormalX=0 NormalY=0 NormalZ=1 AngleXU=0 Radius=29.0625 StartAngle=0.993345 EndAngle=2.14825
    g11: LineSegment StartX=27.4926 StartY=-19.0074 StartZ=0 EndX=24.3502 EndY=-15.8649 EndZ=0
    g12: ArcOfCircle CenterX=23.25 CenterY=-23.25 CenterZ=0 NormalX=0 NormalY=0 NormalZ=1 AngleXU=0 Radius=6 StartAngle=3.92699 EndAngle=7.06858
    g13: LineSegment StartX=15.8649 StartY=-24.3502 StartZ=0 EndX=19.0074 EndY=-27.4926 EndZ=0
    g14: LineSegment [constr] StartX=0 StartY=0 StartZ=0 EndX=0 EndY=29.0625 EndZ=0
    g15: LineSegment StartX=-27.4926 StartY=19.0074 StartZ=0 EndX=-24.3502 EndY=15.8649 EndZ=0
    g16: ArcOfCircle CenterX=-23.25 CenterY=23.25 CenterZ=0 NormalX=0 NormalY=0 NormalZ=1 AngleXU=0 Radius=6 StartAngle=0.785398 EndAngle=3.92699
    g17: LineSegment StartX=-15.8649 StartY=24.3502 StartZ=0 EndX=-19.0074 EndY=27.4926 EndZ=0
    g18: LineSegment StartX=-27.4926 StartY=-19.0074 StartZ=0 EndX=-24.3502 EndY=-15.8649 EndZ=0
    g19: ArcOfCircle CenterX=-23.25 CenterY=-23.25 CenterZ=0 NormalX=0 NormalY=0 NormalZ=1 AngleXU=0 Radius=6 StartAngle=2.35619 EndAngle=5.49779
    g20: LineSegment StartX=-15.8649 StartY=-24.3502 StartZ=0 EndX=-19.0074 EndY=-27.4926 EndZ=0
    g21: ArcOfCircle CenterX=0 CenterY=0 CenterZ=0 NormalX=0 NormalY=0 NormalZ=1 AngleXU=0 Radius=29.0625 StartAngle=2.56414 EndAngle=3.71904
    g22: ArcOfCircle CenterX=0 CenterY=0 CenterZ=0 NormalX=0 NormalY=0 NormalZ=1 AngleXU=0 Radius=29.0625 StartAngle=4.13494 EndAngle=5.28984
    g23: ArcOfCircle CenterX=0 CenterY=0 CenterZ=0 NormalX=0 NormalY=0 NormalZ=1 AngleXU=0 Radius=29.0625 StartAngle=5.70573 EndAngle=6.86064
    g24: Circle CenterX=0 CenterY=0 CenterZ=0 NormalX=0 NormalY=0 NormalZ=1 AngleXU=0 Radius=20
    g25: Circle CenterX=23.25 CenterY=23.25 CenterZ=0 NormalX=0 NormalY=0 NormalZ=1 AngleXU=0 Radius=4
    g26: Circle CenterX=-23.25 CenterY=23.25 CenterZ=0 NormalX=0 NormalY=0 NormalZ=1 AngleXU=0 Radius=4
    g27: Circle CenterX=-23.25 CenterY=-23.25 CenterZ=0 NormalX=0 NormalY=0 NormalZ=1 AngleXU=0 Radius=4
    g28: Circle CenterX=23.25 CenterY=-23.25 CenterZ=0 NormalX=0 NormalY=0 NormalZ=1 AngleXU=0 Radius=4
  constraints (78):
    c: Coincident(g0,g1)
    c: Coincident(g1,g2)
    c: Coincident(g2,g3)
    c: Coincident(g3,g0)
    c: Horizontal(g0)
    c: Horizontal(g2)
    c: Vertical(g1)
    c: Vertical(g3)
    c: Coincident(g0,g4)
    c: Coincident(g4,g-1)
    c: Coincident(g4,g5)
    c: Coincident(g5,g1)
    c: Equal(g5,g4)
    c: Parallel(g5,g4)
    c: Equal(g3,g0)
    c: Parallel(g6,g7)
    c: Coincident(g-1,g8)
    c: Horizontal(g8)
    c: Angle(g8,g6) = 0.785398
    c: Coincident(g9,g0)
    c: Coincident(g9,g6)
    c: Coincident(g10,g-1)
    c: Parallel(g11,g13)
    c: Tangent(g12,g13) = -1.5708
    c: Tangent(g12,g11) = -1.5708
    c: PointOnObject(g11,g10)
    c: PointOnObject(g13,g10)
    c: Perpendicular(g6,g11)
    c: Coincident(g12,g1)
    c: Equal(g11,g6)
    c: Tangent(g9,g7) = 1.5708
    c: Equal(g9,g12)
    c: Coincident(g-1,g14)
    c: Vertical(g14)
    c: PointOnObject(g14,g10)
    c: Parallel(g15,g17)
    c: Parallel(g18,g20)
    c: Tangent(g19,g20) = 1.5708
    c: Tangent(g19,g18) = 1.5708
    c: Perpendicular(g15,g18)
    c: Equal(g18,g15)
    c: Tangent(g16,g17) = -1.5708
    c: Equal(g16,g19)
    c: Perpendicular(g7,g17)
    c: Equal(g12,g19)
    c: Coincident(g19,g2)
    c: Coincident(g0,g16)
    c: PointOnObject(g20,g10)
    c: Tangent(g16,g15) = -1.5708
    c: PointOnObject(g15,g10)
    c: Coincident(g10,g7)
    c: Coincident(g23,g6)
    c: Equal(g10,g21)
    c: Coincident(g10,g17)
    c: Coincident(g10,g21)
    c: Equal(g21,g22)
    c: PointOnObject(g21,g18)
    c: PointOnObject(g22,g20)
    c: Coincident(g21,g22)
    c: Equal(g22,g23)
    c: PointOnObject(g23,g11)
    c: Coincident(g22,g23)
    c: PointOnObject(g22,g13)
    c: PointOnObject(g21,g15)
    c: Coincident(g24,g-1)
    c: Coincident(g25,g0)
    c: Coincident(g26,g0)
    c: Coincident(g27,g2)
    c: Coincident(g28,g1)
    c: Equal(g28,g25)
    c: Equal(g25,g26)
    c: Equal(g26,g27)
    c: DistanceX(g0,g0) = 46.5
    c: Radius(g28) = 4
    c: Radius(g23) = 29.0625
    c: Radius(g24) = 20
    c: Radius(g12) = 6
    c: PointOnObject(g8,g23)
FEATURE [PartDesign::Pad] Pad010
  Length = 197
  Length2 = 100
  Midplane = true
  Placement = pos=(0,0,0) rot=(1,0,0;1.5708rad)
  Profile = -> Sketch013
  Refine = true
  Type = 0
  expr: Length = Medidas.l8 + Medidas.carrera - 2 * Medidas.gg
FEATURE [Sketcher::SketchObject] Sketch014
  ExternalGeometry = -> [Pad010]
  MapMode = 5
  Placement = pos=(0,-98.5,-1.01918e-11) rot=(1,0,0;1.5708rad)
  Support = -> [Pad010]
  expr: Constraints[37] = Medidas.mmm / 2
  expr: Constraints[15] = Medidas.ee
  expr: Constraints[33] = Medidas.tg
  expr: Constraints[32] = Medidas.rt / 2
  sketch-geometry (15):
    g0: LineSegment StartX=-32.5 StartY=32.5 StartZ=0 EndX=32.5 EndY=32.5 EndZ=0
    g1: LineSegment StartX=32.5 StartY=32.5 StartZ=0 EndX=32.5 EndY=-32.5 EndZ=0
    g2: LineSegment StartX=32.5 StartY=-32.5 StartZ=0 EndX=-32.5 EndY=-32.5 EndZ=0
    g3: LineSegment StartX=-32.5 StartY=-32.5 StartZ=0 EndX=-32.5 EndY=32.5 EndZ=0
    g4: LineSegment [constr] StartX=-32.5 StartY=32.5 StartZ=0 EndX=0 EndY=0 EndZ=0
    g5: LineSegment [constr] StartX=0 StartY=0 StartZ=0 EndX=32.5 EndY=-32.5 EndZ=0
    g6: Circle CenterX=-23.25 CenterY=23.25 CenterZ=0 NormalX=0 NormalY=0 NormalZ=1 AngleXU=0 Radius=4
    g7: Circle CenterX=23.25 CenterY=23.25 CenterZ=0 NormalX=0 NormalY=0 NormalZ=1 AngleXU=0 Radius=4
    g8: Circle CenterX=23.25 CenterY=-23.25 CenterZ=0 NormalX=0 NormalY=0 NormalZ=1 AngleXU=0 Radius=4
    g9: Circle CenterX=-23.25 CenterY=-23.25 CenterZ=0 NormalX=0 NormalY=0 NormalZ=1 AngleXU=0 Radius=4
    g10: LineSegment [constr] StartX=-23.25 StartY=23.25 StartZ=0 EndX=23.25 EndY=23.25 EndZ=0
    g11: LineSegment [constr] StartX=23.25 StartY=23.25 StartZ=0 EndX=23.25 EndY=-23.25 EndZ=0
    g12: LineSegment [constr] StartX=23.25 StartY=-23.25 StartZ=0 EndX=-23.25 EndY=-23.25 EndZ=0
    g13: LineSegment [constr] StartX=-23.25 StartY=-23.25 StartZ=0 EndX=-23.25 EndY=23.25 EndZ=0
    g14: Circle CenterX=0 CenterY=0 CenterZ=0 NormalX=0 NormalY=0 NormalZ=1 AngleXU=0 Radius=10
  constraints (38):
    c: Coincident(g0,g1)
    c: Coincident(g1,g2)
    c: Coincident(g2,g3)
    c: Coincident(g3,g0)
    c: Horizontal(g0)
    c: Horizontal(g2)
    c: Vertical(g1)
    c: Vertical(g3)
    c: Coincident(g0,g4)
    c: Coincident(g4,g-1)
    c: Coincident(g4,g5)
    c: Coincident(g5,g1)
    c: Parallel(g5,g4)
    c: Equal(g5,g4)
    c: Equal(g0,g3)
    c: DistanceX(g2,g2) = 65
    c: PointOnObject(g6,g4)
    c: Coincident(g10,g11)
    c: Coincident(g11,g12)
    c: Coincident(g12,g13)
    c: Coincident(g13,g10)
    c: Horizontal(g10)
    c: Horizontal(g12)
    c: Vertical(g11)
    c: Vertical(g13)
    c: Coincident(g10,g6)
    c: Coincident(g11,g8)
    c: Coincident(g7,g10)
    c: Coincident(g12,g9)
    c: Equal(g9,g8)
    c: Equal(g8,g7)
    c: Equal(g7,g6)
    c: Radius(g6) = 4
    c: DistanceX(g10,g10) = 46.5
    c: Equal(g13,g10)
    c: Symmetric(g7,g6,g-2)
    c: Coincident(g14,g-1)
    c: Radius(g14) = 10
FEATURE [PartDesign::Pad] Pad011
  BaseFeature = -> Pad010
  Length = 13.5
  Length2 = 100
  Placement = pos=(0,0,0) rot=(1,0,0;1.5708rad)
  Profile = -> Sketch014
  Refine = true
  Type = 0
  expr: Length = Medidas.gg - Medidas.bg
FEATURE [Sketcher::SketchObject] Sketch015
  ExternalGeometry = -> [Pad011]
  MapMode = 5
  Placement = pos=(0,-112,-1.16066e-11) rot=(1,0,0;1.5708rad)
  Support = -> [Pad011]
  expr: Constraints[114] = Medidas.rt * 1.25 + 4.5
  expr: Constraints[45] = Medidas.tg - 2.5 * Medidas.rt
  expr: Constraints[48] = Medidas.rt * 1.25
  sketch-geometry (37):
    g0: LineSegment StartX=-32.5 StartY=13.25 StartZ=0 EndX=-32.5 EndY=-13.25 EndZ=0
    g1: LineSegment StartX=-32.5 StartY=-13.25 StartZ=0 EndX=-23.25 EndY=-13.25 EndZ=0
    g2: LineSegment StartX=-13.25 StartY=-23.25 StartZ=0 EndX=-13.25 EndY=-32.5 EndZ=0
    g3: LineSegment StartX=-13.25 StartY=-32.5 StartZ=0 EndX=13.25 EndY=-32.5 EndZ=0
    g4: LineSegment StartX=13.25 StartY=-32.5 StartZ=0 EndX=13.25 EndY=-23.25 EndZ=0
    g5: LineSegment StartX=23.25 StartY=-13.25 StartZ=0 EndX=32.5 EndY=-13.25 EndZ=0
    g6: LineSegment StartX=32.5 StartY=-13.25 StartZ=0 EndX=32.5 EndY=13.25 EndZ=0
    g7: LineSegment StartX=32.5 StartY=13.25 StartZ=0 EndX=23.25 EndY=13.25 EndZ=0
    g8: LineSegment StartX=13.25 StartY=23.25 StartZ=0 EndX=13.25 EndY=32.5 EndZ=0
    g9: LineSegment StartX=13.25 StartY=32.5 StartZ=0 EndX=-13.25 EndY=32.5 EndZ=0
    g10: LineSegment StartX=-13.25 StartY=32.5 StartZ=0 EndX=-13.25 EndY=23.25 EndZ=0
    g11: LineSegment StartX=-23.25 StartY=13.25 StartZ=0 EndX=-32.5 EndY=13.25 EndZ=0
    g12: ArcOfCircle CenterX=-23.25 CenterY=23.25 CenterZ=0 NormalX=0 NormalY=0 NormalZ=1 AngleXU=0 Radius=10 StartAngle=4.71239 EndAngle=6.28319
    g13: ArcOfCircle CenterX=-23.25 CenterY=-23.25 CenterZ=0 NormalX=0 NormalY=0 NormalZ=1 AngleXU=0 Radius=10 StartAngle=0 EndAngle=1.5708
    g14: ArcOfCircle CenterX=23.25 CenterY=-23.25 CenterZ=0 NormalX=0 NormalY=0 NormalZ=1 AngleXU=0 Radius=10 StartAngle=1.5708 EndAngle=3.14159
    g15: ArcOfCircle CenterX=23.25 CenterY=23.25 CenterZ=0 NormalX=0 NormalY=0 NormalZ=1 AngleXU=0 Radius=10 StartAngle=3.14159 EndAngle=4.71239
    g16: LineSegment StartX=-8.75 StartY=28 StartZ=0 EndX=-8.75 EndY=23.25 EndZ=0
    g17: LineSegment StartX=-23.25 StartY=8.75 StartZ=0 EndX=-28 EndY=8.75 EndZ=0
    g18: LineSegment StartX=-28 StartY=8.75 StartZ=0 EndX=-28 EndY=-8.75 EndZ=0
    g19: LineSegment StartX=-28 StartY=-8.75 StartZ=0 EndX=-23.25 EndY=-8.75 EndZ=0
    g20: LineSegment StartX=-8.75 StartY=-23.25 StartZ=0 EndX=-8.75 EndY=-28 EndZ=0
    g21: LineSegment StartX=-8.75 StartY=-28 StartZ=0 EndX=8.75 EndY=-28 EndZ=0
    g22: LineSegment StartX=8.75 StartY=-28 StartZ=0 EndX=8.75 EndY=-23.25 EndZ=0
    g23: LineSegment StartX=23.25 StartY=-8.75 StartZ=0 EndX=28 EndY=-8.75 EndZ=0
    g24: LineSegment StartX=28 StartY=-8.75 StartZ=0 EndX=28 EndY=8.75 EndZ=0
    g25: LineSegment StartX=28 StartY=8.75 StartZ=0 EndX=23.25 EndY=8.75 EndZ=0
    g26: LineSegment StartX=8.75 StartY=23.25 StartZ=0 EndX=8.75 EndY=28 EndZ=0
    g27: LineSegment StartX=8.75 StartY=28 StartZ=0 EndX=-8.75 EndY=28 EndZ=0
    g28: LineSegment [constr] StartX=-28 StartY=-8.75 StartZ=0 EndX=-32.5 EndY=-8.75 EndZ=0
    g29: LineSegment [constr] StartX=28 StartY=-8.75 StartZ=0 EndX=32.5 EndY=-8.75 EndZ=0
    g30: LineSegment [constr] StartX=-8.75 StartY=28 StartZ=0 EndX=-8.75 EndY=32.5 EndZ=0
    g31: LineSegment [constr] StartX=-8.75 StartY=-28 StartZ=0 EndX=-8.75 EndY=-32.5 EndZ=0
    g32: LineSegment [constr] StartX=-28 StartY=-8.75 StartZ=0 EndX=-28 EndY=-13.25 EndZ=0
    g33: ArcOfCircle CenterX=-23.25 CenterY=23.25 CenterZ=0 NormalX=0 NormalY=0 NormalZ=1 AngleXU=0 Radius=14.5 StartAngle=4.71239 EndAngle=6.28319
    g34: ArcOfCircle CenterX=23.25 CenterY=23.25 CenterZ=0 NormalX=0 NormalY=0 NormalZ=1 AngleXU=0 Radius=14.5 StartAngle=3.14159 EndAngle=4.71239
    g35: ArcOfCircle CenterX=23.25 CenterY=-23.25 CenterZ=0 NormalX=0 NormalY=0 NormalZ=1 AngleXU=0 Radius=14.5 StartAngle=1.5708 EndAngle=3.14159
    g36: ArcOfCircle CenterX=-23.25 CenterY=-23.25 CenterZ=0 NormalX=0 NormalY=0 NormalZ=1 AngleXU=0 Radius=14.5 StartAngle=0 EndAngle=1.5708
  constraints (115):
    c: Coincident(g1,g0)
    c: Horizontal(g1)
    c: Vertical(g2)
    c: Coincident(g2,g3)
    c: Coincident(g3,g4)
    c: Vertical(g4)
    c: Horizontal(g5)
    c: Coincident(g5,g6)
    c: Coincident(g6,g7)
    c: Vertical(g8)
    c: Coincident(g8,g9)
    c: Horizontal(g9)
    c: Coincident(g9,g10)
    c: Coincident(g11,g0)
    c: Horizontal(g11)
    c: PointOnObject(g0,g-3)
    c: Symmetric(g0,g0,g-1)
    c: Symmetric(g6,g5,g-1)
    c: Symmetric(g8,g9,g-2)
    c: PointOnObject(g9,g-4)
    c: Vertical(g10)
    c: Horizontal(g7)
    c: Symmetric(g3,g2,g-2)
    c: PointOnObject(g3,g-6)
    c: Equal(g10,g8)
    c: Equal(g8,g7)
    c: Equal(g7,g5)
    c: Equal(g5,g4)
    c: Equal(g4,g2)
    c: Equal(g2,g1)
    c: Equal(g1,g11)
    c: Equal(g3,g0)
    c: Equal(g0,g9)
    c: Equal(g9,g6)
    c: Coincident(g12,g10)
    c: Coincident(g12,g11)
    c: Coincident(g13,g1)
    c: Coincident(g13,g2)
    c: Coincident(g14,g4)
    c: Coincident(g14,g5)
    c: Coincident(g15,g7)
    c: Coincident(g15,g8)
    c: Equal(g15,g12)
    c: Equal(g12,g13)
    c: Equal(g13,g14)
    c: DistanceX(g3,g3) = 26.5
    c: Vertical(g1,g13)
    c: PointOnObject(g6,g-5)
    c: Radius(g13) = 10
    c: Vertical(g16)
    c: Coincident(g17,g18)
    c: Vertical(g18)
    c: Coincident(g18,g19)
    c: Horizontal(g19)
    c: Vertical(g20)
    c: Coincident(g20,g21)
    c: Horizontal(g21)
    c: Coincident(g21,g22)
    c: Vertical(g22)
    c: Horizontal(g23)
    c: Coincident(g23,g24)
    c: Vertical(g24)
    c: Coincident(g24,g25)
    c: Horizontal(g25)
    c: Vertical(g26)
    c: Coincident(g26,g27)
    c: Coincident(g27,g16)
    c: Horizontal(g27)
    c: Symmetric(g26,g16,g-2)
    c: Symmetric(g17,g18,g-1)
    c: Symmetric(g20,g21,g-2)
    c: Symmetric(g23,g24,g-1)
    c: Equal(g24,g27)
    c: Equal(g27,g18)
    c: Equal(g18,g21)
    c: Equal(g20,g22)
    c: Equal(g22,g23)
    c: Equal(g23,g25)
    c: Equal(g25,g26)
    c: Equal(g26,g16)
    c: Equal(g16,g17)
    c: Equal(g17,g19)
    c: Horizontal(g17)
    c: Coincident(g18,g28)
    c: PointOnObject(g28,g0)
    c: Horizontal(g28)
    c: Coincident(g23,g29)
    c: PointOnObject(g29,g6)
    c: Horizontal(g29)
    c: Coincident(g16,g30)
    c: PointOnObject(g30,g9)
    c: Vertical(g30)
    c: Coincident(g20,g31)
    c: Vertical(g31)
    c: Equal(g29,g31)
    c: Equal(g31,g28)
    c: Equal(g28,g30)
    c: DistanceX(g28,g28) = 4.5
    c: Vertical(g32)
    c: PointOnObject(g32,g1)
    c: Coincident(g18,g32)
    c: Equal(g32,g28)
    c: PointOnObject(g31,g3)
    c: Coincident(g33,g16)
    c: Coincident(g33,g17)
    c: Coincident(g34,g25)
    c: Coincident(g34,g26)
    c: Coincident(g35,g22)
    c: Coincident(g35,g23)
    c: Tangent(g36,g19) = 1.5708
    c: Tangent(g36,g20) = 1.5708
    c: Vertical(g35,g23)
    c: Equal(g33,g34)
    c: Equal(g34,g35)
    c: Radius(g35) = 14.5
FEATURE [PartDesign::Pad] Pad012
  BaseFeature = -> Pad011
  Length = 16
  Length2 = 100
  Placement = pos=(0,0,0) rot=(1,0,0;1.5708rad)
  Profile = -> Sketch015
  Refine = true
  Type = 0
  expr: Length = Medidas.bg
FEATURE [Sketcher::SketchObject] Sketch016
  MapMode = 5
  Placement = pos=(0,-112,-1.16066e-11) rot=(1,0,0;1.5708rad)
  Support = -> [Pad012]
  expr: Constraints[3] = Medidas.b / 2 * 1.1
  expr: Constraints[2] = Medidas.mmm / 2
  sketch-geometry (2):
    g0: Circle CenterX=0 CenterY=0 CenterZ=0 NormalX=0 NormalY=0 NormalZ=1 AngleXU=0 Radius=10
    g1: Circle CenterX=0 CenterY=0 CenterZ=0 NormalX=0 NormalY=0 NormalZ=1 AngleXU=0 Radius=22
  constraints (4):
    c: Coincident(g0,g-1)
    c: Coincident(g1,g-1)
    c: Radius(g0) = 10
    c: Radius(g1) = 22
FEATURE [PartDesign::Pad] Pad013
  BaseFeature = -> Pad012
  Length = 22
  Length2 = 100
  Placement = pos=(0,0,0) rot=(1,0,0;1.5708rad)
  Profile = -> Sketch016
  Refine = true
  Type = 0
  expr: Length = Medidas.bg + Medidas.vd
FEATURE [Sketcher::SketchObject] Sketch017
  MapMode = 5
  Placement = pos=(0,-134,-1.38931e-11) rot=(1,0,0;1.5708rad)
  Support = -> [Pad013]
  expr: Constraints[3] = Medidas.mmm / 2
  expr: Constraints[2] = Medidas.b / 2
  sketch-geometry (2):
    g0: Circle CenterX=0 CenterY=0 CenterZ=0 NormalX=0 NormalY=0 NormalZ=1 AngleXU=0 Radius=20
    g1: Circle CenterX=0 CenterY=0 CenterZ=0 NormalX=0 NormalY=0 NormalZ=1 AngleXU=0 Radius=10
  constraints (4):
    c: Coincident(g0,g-1)
    c: Coincident(g1,g-1)
    c: Radius(g0) = 20
    c: Radius(g1) = 10
FEATURE [PartDesign::Pad] Pad014
  BaseFeature = -> Pad013
  Length = 20.5
  Length2 = 100
  Placement = pos=(0,0,0) rot=(1,0,0;1.5708rad)
  Profile = -> Sketch017
  Refine = true
  Type = 0
  expr: Length = Medidas.l2 - Medidas.vd
FEATURE [PartDesign::Mirrored] Mirrored002
  BaseFeature = -> Pad014
  MirrorPlane = -> XZ_Plane005
  Originals = -> [Pad011]
  Placement = pos=(0,0,0) rot=(1,0,0;1.5708rad)
  Refine = true
FEATURE [PartDesign::Mirrored] Mirrored003
  BaseFeature = -> Mirrored002
  MirrorPlane = -> XZ_Plane005
  Originals = -> [Pad012]
  Placement = pos=(0,0,0) rot=(1,0,0;1.5708rad)
  Refine = true
FEATURE [Sketcher::SketchObject] Sketch018
  MapMode = 5
  Placement = pos=(0,112,1.15718e-11) rot=(-1,0,0;1.5708rad)
  Support = -> [Mirrored003]
  expr: Constraints[1] = Medidas.b / 2
  sketch-geometry (1):
    g0: Circle CenterX=0 CenterY=0 CenterZ=0 NormalX=0 NormalY=0 NormalZ=1 AngleXU=0 Radius=20
  constraints (2):
    c: Coincident(g0,g-1)
    c: Radius(g0) = 20
FEATURE [PartDesign::Pad] Pad015
  BaseFeature = -> Mirrored003
  Length = 20
  Length2 = 100
  Placement = pos=(0,0,0) rot=(1,0,0;1.5708rad)
  Profile = -> Sketch018
  Refine = true
  Type = 0
  expr: Length = Medidas.bg + Medidas.va
FEATURE [PartDesign::Fillet] Fillet001
  Base = -> Pad015 [Edge27,Edge21,Edge39,Edge213,Edge201,Edge200,Edge28,Edge207]
  BaseFeature = -> Pad015
  Placement = pos=(0,0,0) rot=(1,0,0;1.5708rad)
  Radius = 4
  expr: Radius = Medidas.rt / 2
FEATURE [PartDesign::Chamfer] Chamfer001
  Base = -> Fillet001 [Edge306]
  BaseFeature = -> Fillet001
  Placement = pos=(0,0,0) rot=(1,0,0;1.5708rad)
  Size = 2
FEATURE [Sketcher::SketchObject] Sketch019
  ExternalGeometry = -> [Chamfer001]
  MapMode = 5
  Placement = pos=(0,-3.34e-12,32.5) rot=(0,0,1;3.14159rad)
  Support = -> [Chamfer001]
  expr: Constraints[5] = Medidas.pl
  expr: Constraints[4] = Medidas.pl
  expr: Constraints[3] = Medidas.eee / 2
  sketch-geometry (2):
    g0: Circle CenterX=0 CenterY=116.5 CenterZ=0 NormalX=0 NormalY=0 NormalZ=1 AngleXU=0 Radius=5.5
    g1: Circle CenterX=0 CenterY=-116.5 CenterZ=0 NormalX=0 NormalY=0 NormalZ=1 AngleXU=0 Radius=5.5
  constraints (6):
    c: PointOnObject(g0,g-2)
    c: PointOnObject(g1,g-2)
    c: Equal(g1,g0)
    c: Radius(g0) = 5.5
    c: DistanceY(g0,g-4) = 11.5
    c: DistanceY(g-3,g1) = 11.5
FEATURE [PartDesign::Pocket] Pocket002
  BaseFeature = -> Chamfer001
  Length = 20
  Length2 = 100
  Placement = pos=(0,0,0) rot=(1,0,0;1.5708rad)
  Profile = -> Sketch019
  Refine = true
  Type = 0
  expr: Length = Medidas.b / 2
FEATURE [Sketcher::SketchObject] Sketch020
  ExternalGeometry = -> [Pocket002]
  MapMode = 5
  Placement = pos=(0,-3.355e-12,32.5) rot=(0,0,1;3.14159rad)
  Support = -> [Pocket002]
  expr: Constraints[6] = Medidas.eee * 3 / 4
  expr: Constraints[5] = Medidas.eee / 2
  sketch-geometry (4):
    g0: Circle CenterX=0 CenterY=116.5 CenterZ=0 NormalX=0 NormalY=0 NormalZ=1 AngleXU=0 Radius=5.5
    g1: Circle CenterX=0 CenterY=116.5 CenterZ=0 NormalX=0 NormalY=0 NormalZ=1 AngleXU=0 Radius=7.36151
    g2: Circle CenterX=0 CenterY=-116.5 CenterZ=0 NormalX=0 NormalY=0 NormalZ=1 AngleXU=0 Radius=5.5
    g3: Circle CenterX=0 CenterY=-116.5 CenterZ=0 NormalX=0 NormalY=0 NormalZ=1 AngleXU=0 Radius=8.25
  constraints (7):
    c: PointOnObject(g0,g-2)
    c: Coincident(g1,g-4)
    c: Coincident(g0,g1)
    c: Coincident(g-3,g3)
    c: Coincident(g3,g2)
    c: Radius(g2) = 5.5
    c: Radius(g3) = 8.25
FEATURE [PartDesign::Pad] Pad016
  BaseFeature = -> Pocket002
  Length = 20
  Length2 = 100
  Placement = pos=(0,0,0) rot=(1,0,0;1.5708rad)
  Profile = -> Sketch020
  Refine = true
  Reversed = true
  Type = 0
  expr: Length = Medidas.b / 2
FEATURE [PartDesign::Body] Body003  label="Barrel+Endcap001"
  Group = -> [Sketch013,Pad010,Sketch014,Pad011,Sketch015,Pad012,Sketch016,Pad013,Sketch017,Pad014,Mirrored002,Mirrored003,Sketch018,Pad015,Fillet001,Chamfer001,Sketch019,Pocket002,Sketch020,Pad016]
  Origin = -> Origin005
  Tip = -> Pad016
FEATURE [Sketcher::SketchObject] Sketch021
  MapMode = 5
  Placement = pos=(0,0,0) rot=(1,0,0;1.5708rad)
  Support = -> [XZ_Plane006]
  expr: Constraints[1] = Medidas.b / 2 * 0.95
  sketch-geometry (1):
    g0: Circle CenterX=0 CenterY=0 CenterZ=0 NormalX=0 NormalY=0 NormalZ=1 AngleXU=0 Radius=19
  constraints (2):
    c: Coincident(g0,g-1)
    c: Radius(g0) = 19
FEATURE [PartDesign::Pad] Pad017
  Length = 10
  Length2 = 100
  Placement = pos=(0,0,0) rot=(1,0,0;1.5708rad)
  Profile = -> Sketch021
  Refine = true
  Type = 0
FEATURE [Sketcher::SketchObject] Sketch022
  MapMode = 5
  Placement = pos=(0,0,0) rot=(-1,0,0;1.5708rad)
  Support = -> [Pad017]
  expr: Constraints[1] = Medidas.mmm / 2
  sketch-geometry (1):
    g0: Circle CenterX=0 CenterY=0 CenterZ=0 NormalX=0 NormalY=0 NormalZ=1 AngleXU=0 Radius=10
  constraints (2):
    c: Coincident(g0,g-1)
    c: Radius(g0) = 10
FEATURE [PartDesign::Pad] Pad018
  BaseFeature = -> Pad017
  Length = 256
  Length2 = 100
  Placement = pos=(0,0,0) rot=(1,0,0;1.5708rad)
  Profile = -> Sketch022
  Refine = true
  Reversed = true
  Type = 0
  expr: Length = Medidas.l8 + Medidas.carrera
FEATURE [Sketcher::SketchObject] Sketch023
  MapMode = 5
  Placement = pos=(0,-256,-2.64883e-11) rot=(1,0,0;1.5708rad)
  Support = -> [Pad018]
  expr: Constraints[22] = Medidas.sw
  expr: Constraints[19] = Medidas.sw
  sketch-geometry (8):
    g0: LineSegment StartX=-25.5 StartY=8.5 StartZ=0 EndX=-8.5 EndY=8.5 EndZ=0
    g1: LineSegment StartX=-8.5 StartY=8.5 StartZ=0 EndX=-8.5 EndY=-8.5 EndZ=0
    g2: LineSegment StartX=-8.5 StartY=-8.5 StartZ=0 EndX=-25.5 EndY=-8.5 EndZ=0
    g3: LineSegment StartX=-25.5 StartY=-8.5 StartZ=0 EndX=-25.5 EndY=8.5 EndZ=0
    g4: LineSegment StartX=25.5 StartY=8.5 StartZ=0 EndX=8.5 EndY=8.5 EndZ=0
    g5: LineSegment StartX=8.5 StartY=8.5 StartZ=0 EndX=8.5 EndY=-8.5 EndZ=0
    g6: LineSegment StartX=8.5 StartY=-8.5 StartZ=0 EndX=25.5 EndY=-8.5 EndZ=0
    g7: LineSegment StartX=25.5 StartY=-8.5 StartZ=0 EndX=25.5 EndY=8.5 EndZ=0
  constraints (23):
    c: Coincident(g0,g1)
    c: Coincident(g1,g2)
    c: Coincident(g2,g3)
    c: Coincident(g3,g0)
    c: Horizontal(g0)
    c: Horizontal(g2)
    c: Vertical(g1)
    c: Vertical(g3)
    c: Coincident(g4,g5)
    c: Coincident(g5,g6)
    c: Coincident(g6,g7)
    c: Coincident(g7,g4)
    c: Horizontal(g4)
    c: Horizontal(g6)
    c: Vertical(g5)
    c: Vertical(g7)
    c: Symmetric(g0,g4,g-2)
    c: Equal(g5,g1)
    c: Equal(g6,g2)
    c: DistanceX(g0,g4) = 17
    c: Symmetric(g0,g2,g-1)
    c: Equal(g0,g3)
    c: DistanceX(g0,g0) = 17
FEATURE [PartDesign::Pocket] Pocket003
  BaseFeature = -> Pad018
  Length = 8
  Length2 = 100
  Placement = pos=(0,0,0) rot=(1,0,0;1.5708rad)
  Profile = -> Sketch023
  Refine = true
  Type = 0
  expr: Length = Medidas.kw
FEATURE [Sketcher::SketchObject] Sketch024
  MapMode = 5
  Placement = pos=(0,-256,-2.64883e-11) rot=(1,0,0;1.5708rad)
  Support = -> [Pocket003]
  expr: Constraints[1] = Medidas.kk / 2
  sketch-geometry (1):
    g0: Circle CenterX=0 CenterY=0 CenterZ=0 NormalX=0 NormalY=0 NormalZ=1 AngleXU=0 Radius=8
  constraints (2):
    c: Coincident(g0,g-1)
    c: Radius(g0) = 8
FEATURE [Part::Helix] Helix001  label="Thread Helice001"
  Angle = 0
  AttacherType = Attacher::AttachEngine3D
  Height = 32
  LocalCoord = 0
  Pitch = 1.5
  Placement = pos=(0,0,0) rot=(-1,0,0;1.5708rad)
  Radius = 8
  Style = 1
  expr: Radius = Medidas.kk / 2
  expr: Height = Medidas.am
  expr: Pitch = Medidas.kkp
FEATURE [App::MeasureDistance] Distance  label="WH"
  Distance = 43.5
  P1 = (0,-171.5,0)
  P2 = (0,-128,0)
  expr: P2.y = -(Medidas.l8 + Medidas.carrera) / 2
FEATURE [Sketcher::SketchObject] Sketch025
  MapMode = 5
  Support = -> [XY_Plane007]
  expr: Constraints[6] = Medidas.kk / 2 * 0.96
  sketch-geometry (3):
    g0: LineSegment StartX=7.68 StartY=0.4 StartZ=0 EndX=7.68 EndY=-0.4 EndZ=0
    g1: LineSegment StartX=7.68 StartY=-0.4 StartZ=0 EndX=8.68 EndY=0 EndZ=0
    g2: LineSegment StartX=8.68 StartY=0 StartZ=0 EndX=7.68 EndY=0.4 EndZ=0
  constraints (9):
    c: Vertical(g0)
    c: Coincident(g0,g1)
    c: PointOnObject(g1,g-1)
    c: Coincident(g1,g2)
    c: Coincident(g2,g0)
    c: Symmetric(g0,g0,g-1)
    c: DistanceX(g-1,g0) = 7.68
    c: DistanceX(g0,g1) = 1
    c: DistanceY(g0,g0) = 0.8
FEATURE [PartDesign::ShapeBinder] ReferenceHelix002  label="ReferenceHelix001"
  Placement = pos=(0,0,0) rot=(-1,0,0;1.5708rad)
  Support = -> [Helix001]
  TraceSupport = false
FEATURE [PartDesign::AdditivePipe] AdditivePipe001
  AuxilleryCurvelinear = true
  AuxillerySpineTangent = false
  Binormal = (0,0,0)
  Mode = 2
  Profile = -> Sketch025
  Refine = true
  Spine = -> ReferenceHelix002 [Edge1,Edge2,Edge3,Edge4,Edge5,Edge6,Edge7,Edge8,Edge9,Edge10,Edge11,Edge12,Edge13,Edge14,Edge15,Edge16,Edge17,Edge18,Edge19,Edge20]
  SpineTangent = false
  Transformation = 0
  Transition = 0
FEATURE [PartDesign::Body] Body005  label="Thread001"
  Group = -> [Sketch025,AdditivePipe001,ReferenceHelix002]
  Origin = -> Origin007
  Placement = pos=(0,-285.5,0) rot=(0,0,1;0rad)
  Tip = -> AdditivePipe001
  expr: Placement.Base.y = -Medidas.l8 - Medidas.carrera - Medidas.l2 - 3
FEATURE [PartDesign::Pad] Pad019
  BaseFeature = -> Pocket003
  Length = 32
  Length2 = 100
  Placement = pos=(0,0,0) rot=(1,0,0;1.5708rad)
  Profile = -> Sketch024
  Refine = true
  Type = 0
  expr: Length = Medidas.am
FEATURE [PartDesign::Body] Body004  label="Piston+rod001"
  Group = -> [Sketch021,Pad017,Sketch022,Pad018,Sketch023,Pocket003,Sketch024,Pad019]
  Origin = -> Origin006
  Tip = -> Pad019
FEATURE [Part::Fuse] Fusion001  label="Piston Rod001"
  Base = -> Body004
  Placement = pos=(0,93.5,0) rot=(0,0,1;0rad)
  Refine = true
  Tool = -> Body005
  expr: Placement.Base.y = (Medidas.l8 + Medidas.carrera) / 2 - Medidas.gg + -Medidas.delta
FEATURE [App::Part] Part001
  Group = -> [Body003,Body004,Helix001,Body005,Fusion001]
  Id = DA-XX-XXX-TCA
  License = CC BY 3.0
  LicenseURL = http://creativecommons.org/licenses/by/3.0/
  Origin = -> Origin004
  Placement = pos=(95,0,0) rot=(0,0,1;0rad)
  Type = Pneumatic cylinder
FEATURE [Spreadsheet::Sheet] Spreadsheet002  label="Medidas002"
  cells = A1=Medidas Tabla; A2=CARRERRA001; B2(carrera)=150; C2=Delta Carrera; D2(delta)=5; A3=Ø; B3(diametro)=63; A4=AM; B4(am)=32; A5=B; B5(b)=45; A6=BG; B6(bg)=16; A7=EE; B7(ee)=75; A8=EEE; B8(eee)=15; C8=1/4 NPT; A9=GG; B9(gg)=36; A10=KK; B10(kk)=16; C10(kkp)=1.5; A11=KV; B11(kv)=24; A12=KW; B12(kw)=8; A13=L2; B13(l2)=26.5; A14=L8; B14(l8)=121; A15=MMM; B15(mmm)=20; A16=PL; B16(pl)=14; A17=RT; B17(rt)=8; A18=SW; B18(sw)=17; A19=TG; B19(tg)=56.5; A20=VA; B20(va)=4; A21=VD; B21(vd)=6; A22=VF; B22(vf)=16; A23=VG; B23(vg)=69; A24=WH; B24(wh)=37; A25=XD; B25(xd)=190; A26=AH; B26(ah)=50; A27=SA; B27(sa)=185; A28=XA; B28(xa)=190; A29=Peso Carrera 0; B29=1600; A30=(gr.) Cada 10mm; B30=60; A31=Peso Total; B31==B29 + B2 / 10 * B30
FEATURE [Sketcher::SketchObject] Sketch026
  MapMode = 5
  Placement = pos=(0,0,0) rot=(1,0,0;1.5708rad)
  Support = -> [XZ_Plane009]
  expr: Constraints[76] = Medidas.rt / 2 * 1.5
  expr: Constraints[72] = Medidas.tg
  expr: Constraints[74] = Medidas.tg * 0.625
  expr: Constraints[75] = Medidas.b / 2
  expr: Constraints[73] = Medidas.rt / 2
  sketch-geometry (29):
    g0: LineSegment [constr] StartX=-28.25 StartY=28.25 StartZ=0 EndX=28.25 EndY=28.25 EndZ=0
    g1: LineSegment [constr] StartX=28.25 StartY=28.25 StartZ=0 EndX=28.25 EndY=-28.25 EndZ=0
    g2: LineSegment [constr] StartX=28.25 StartY=-28.25 StartZ=0 EndX=-28.25 EndY=-28.25 EndZ=0
    g3: LineSegment [constr] StartX=-28.25 StartY=-28.25 StartZ=0 EndX=-28.25 EndY=28.25 EndZ=0
    g4: LineSegment [constr] StartX=-28.25 StartY=28.25 StartZ=0 EndX=0 EndY=0 EndZ=0
    g5: LineSegment [constr] StartX=0 StartY=0 StartZ=0 EndX=28.25 EndY=-28.25 EndZ=0
    g6: LineSegment StartX=32.4926 StartY=24.0074 StartZ=0 EndX=28.8493 EndY=20.364 EndZ=0
    g7: LineSegment StartX=20.364 StartY=28.8493 StartZ=0 EndX=24.0074 EndY=32.4926 EndZ=0
    g8: LineSegment [constr] StartX=0 StartY=0 StartZ=0 EndX=35.3125 EndY=0 EndZ=0
    g9: ArcOfCircle CenterX=28.25 CenterY=28.25 CenterZ=0 NormalX=0 NormalY=0 NormalZ=1 AngleXU=0 Radius=6 StartAngle=5.49779 EndAngle=8.63938
    g10: ArcOfCircle CenterX=0 CenterY=0 CenterZ=0 NormalX=0 NormalY=0 NormalZ=1 AngleXU=0 Radius=35.3125 StartAngle=0.956138 EndAngle=2.18545
    g11: LineSegment StartX=32.4926 StartY=-24.0074 StartZ=0 EndX=28.8493 EndY=-20.364 EndZ=0
    g12: ArcOfCircle CenterX=28.25 CenterY=-28.25 CenterZ=0 NormalX=0 NormalY=0 NormalZ=1 AngleXU=0 Radius=6 StartAngle=3.92699 EndAngle=7.06858
    g13: LineSegment StartX=20.364 StartY=-28.8493 StartZ=0 EndX=24.0074 EndY=-32.4926 EndZ=0
    g14: LineSegment [constr] StartX=0 StartY=0 StartZ=0 EndX=0 EndY=35.3125 EndZ=0
    g15: LineSegment StartX=-32.4926 StartY=24.0074 StartZ=0 EndX=-28.8493 EndY=20.364 EndZ=0
    g16: ArcOfCircle CenterX=-28.25 CenterY=28.25 CenterZ=0 NormalX=0 NormalY=0 NormalZ=1 AngleXU=0 Radius=6 StartAngle=0.785398 EndAngle=3.92699
    g17: LineSegment StartX=-20.364 StartY=28.8493 StartZ=0 EndX=-24.0074 EndY=32.4926 EndZ=0
    g18: LineSegment StartX=-32.4926 StartY=-24.0074 StartZ=0 EndX=-28.8493 EndY=-20.364 EndZ=0
    g19: ArcOfCircle CenterX=-28.25 CenterY=-28.25 CenterZ=0 NormalX=0 NormalY=0 NormalZ=1 AngleXU=0 Radius=6 StartAngle=2.35619 EndAngle=5.49779
    g20: LineSegment StartX=-20.364 StartY=-28.8493 StartZ=0 EndX=-24.0074 EndY=-32.4926 EndZ=0
    g21: ArcOfCircle CenterX=0 CenterY=0 CenterZ=0 NormalX=0 NormalY=0 NormalZ=1 AngleXU=0 Radius=35.3125 StartAngle=2.52693 EndAngle=3.75625
    g22: ArcOfCircle CenterX=0 CenterY=0 CenterZ=0 NormalX=0 NormalY=0 NormalZ=1 AngleXU=0 Radius=35.3125 StartAngle=4.09773 EndAngle=5.32705
    g23: ArcOfCircle CenterX=0 CenterY=0 CenterZ=0 NormalX=0 NormalY=0 NormalZ=1 AngleXU=0 Radius=35.3125 StartAngle=5.66853 EndAngle=6.89784
    g24: Circle CenterX=0 CenterY=0 CenterZ=0 NormalX=0 NormalY=0 NormalZ=1 AngleXU=0 Radius=22.5
    g25: Circle CenterX=28.25 CenterY=28.25 CenterZ=0 NormalX=0 NormalY=0 NormalZ=1 AngleXU=0 Radius=4
    g26: Circle CenterX=-28.25 CenterY=28.25 CenterZ=0 NormalX=0 NormalY=0 NormalZ=1 AngleXU=0 Radius=4
    g27: Circle CenterX=-28.25 CenterY=-28.25 CenterZ=0 NormalX=0 NormalY=0 NormalZ=1 AngleXU=0 Radius=4
    g28: Circle CenterX=28.25 CenterY=-28.25 CenterZ=0 NormalX=0 NormalY=0 NormalZ=1 AngleXU=0 Radius=4
  constraints (78):
    c: Coincident(g0,g1)
    c: Coincident(g1,g2)
    c: Coincident(g2,g3)
    c: Coincident(g3,g0)
    c: Horizontal(g0)
    c: Horizontal(g2)
    c: Vertical(g1)
    c: Vertical(g3)
    c: Coincident(g0,g4)
    c: Coincident(g4,g-1)
    c: Coincident(g4,g5)
    c: Coincident(g5,g1)
    c: Equal(g5,g4)
    c: Parallel(g5,g4)
    c: Equal(g3,g0)
    c: Parallel(g6,g7)
    c: Coincident(g-1,g8)
    c: Horizontal(g8)
    c: Angle(g8,g6) = 0.785398
    c: Coincident(g9,g0)
    c: Coincident(g9,g6)
    c: Coincident(g10,g-1)
    c: Parallel(g11,g13)
    c: Tangent(g12,g13) = -1.5708
    c: Tangent(g12,g11) = -1.5708
    c: PointOnObject(g11,g10)
    c: PointOnObject(g13,g10)
    c: Perpendicular(g6,g11)
    c: Coincident(g12,g1)
    c: Equal(g11,g6)
    c: Tangent(g9,g7) = 1.5708
    c: Equal(g9,g12)
    c: Coincident(g-1,g14)
    c: Vertical(g14)
    c: PointOnObject(g14,g10)
    c: Parallel(g15,g17)
    c: Parallel(g18,g20)
    c: Tangent(g19,g20) = 1.5708
    c: Tangent(g19,g18) = 1.5708
    c: Perpendicular(g15,g18)
    c: Equal(g18,g15)
    c: Tangent(g16,g17) = -1.5708
    c: Equal(g16,g19)
    c: Perpendicular(g7,g17)
    c: Equal(g12,g19)
    c: Coincident(g19,g2)
    c: Coincident(g0,g16)
    c: PointOnObject(g20,g10)
    c: Tangent(g16,g15) = -1.5708
    c: PointOnObject(g15,g10)
    c: Coincident(g10,g7)
    c: Coincident(g23,g6)
    c: Equal(g10,g21)
    c: Coincident(g10,g17)
    c: Coincident(g10,g21)
    c: Equal(g21,g22)
    c: PointOnObject(g21,g18)
    c: PointOnObject(g22,g20)
    c: Coincident(g21,g22)
    c: Equal(g22,g23)
    c: PointOnObject(g23,g11)
    c: Coincident(g22,g23)
    c: PointOnObject(g22,g13)
    c: PointOnObject(g21,g15)
    c: Coincident(g24,g-1)
    c: Coincident(g25,g0)
    c: Coincident(g26,g0)
    c: Coincident(g27,g2)
    c: Coincident(g28,g1)
    c: Equal(g28,g25)
    c: Equal(g25,g26)
    c: Equal(g26,g27)
    c: DistanceX(g0,g0) = 56.5
    c: Radius(g28) = 4
    c: Radius(g23) = 35.3125
    c: Radius(g24) = 22.5
    c: Radius(g12) = 6
    c: PointOnObject(g8,g23)
FEATURE [PartDesign::Pad] Pad020
  Length = 199
  Length2 = 100
  Midplane = true
  Placement = pos=(0,0,0) rot=(1,0,0;1.5708rad)
  Profile = -> Sketch026
  Refine = true
  Type = 0
  expr: Length = Medidas.l8 + Medidas.carrera - 2 * Medidas.gg
FEATURE [Sketcher::SketchObject] Sketch027
  ExternalGeometry = -> [Pad020]
  MapMode = 5
  Placement = pos=(0,-99.5,-1.02953e-11) rot=(1,0,0;1.5708rad)
  Support = -> [Pad020]
  expr: Constraints[37] = Medidas.mmm / 2
  expr: Constraints[15] = Medidas.ee
  expr: Constraints[33] = Medidas.tg
  expr: Constraints[32] = Medidas.rt / 2
  sketch-geometry (15):
    g0: LineSegment StartX=-37.5 StartY=37.5 StartZ=0 EndX=37.5 EndY=37.5 EndZ=0
    g1: LineSegment StartX=37.5 StartY=37.5 StartZ=0 EndX=37.5 EndY=-37.5 EndZ=0
    g2: LineSegment StartX=37.5 StartY=-37.5 StartZ=0 EndX=-37.5 EndY=-37.5 EndZ=0
    g3: LineSegment StartX=-37.5 StartY=-37.5 StartZ=0 EndX=-37.5 EndY=37.5 EndZ=0
    g4: LineSegment [constr] StartX=-37.5 StartY=37.5 StartZ=0 EndX=0 EndY=0 EndZ=0
    g5: LineSegment [constr] StartX=0 StartY=0 StartZ=0 EndX=37.5 EndY=-37.5 EndZ=0
    g6: Circle CenterX=-28.25 CenterY=28.25 CenterZ=0 NormalX=0 NormalY=0 NormalZ=1 AngleXU=0 Radius=4
    g7: Circle CenterX=28.25 CenterY=28.25 CenterZ=0 NormalX=0 NormalY=0 NormalZ=1 AngleXU=0 Radius=4
    g8: Circle CenterX=28.25 CenterY=-28.25 CenterZ=0 NormalX=0 NormalY=0 NormalZ=1 AngleXU=0 Radius=4
    g9: Circle CenterX=-28.25 CenterY=-28.25 CenterZ=0 NormalX=0 NormalY=0 NormalZ=1 AngleXU=0 Radius=4
    g10: LineSegment [constr] StartX=-28.25 StartY=28.25 StartZ=0 EndX=28.25 EndY=28.25 EndZ=0
    g11: LineSegment [constr] StartX=28.25 StartY=28.25 StartZ=0 EndX=28.25 EndY=-28.25 EndZ=0
    g12: LineSegment [constr] StartX=28.25 StartY=-28.25 StartZ=0 EndX=-28.25 EndY=-28.25 EndZ=0
    g13: LineSegment [constr] StartX=-28.25 StartY=-28.25 StartZ=0 EndX=-28.25 EndY=28.25 EndZ=0
    g14: Circle CenterX=0 CenterY=0 CenterZ=0 NormalX=0 NormalY=0 NormalZ=1 AngleXU=0 Radius=10
  constraints (38):
    c: Coincident(g0,g1)
    c: Coincident(g1,g2)
    c: Coincident(g2,g3)
    c: Coincident(g3,g0)
    c: Horizontal(g0)
    c: Horizontal(g2)
    c: Vertical(g1)
    c: Vertical(g3)
    c: Coincident(g0,g4)
    c: Coincident(g4,g-1)
    c: Coincident(g4,g5)
    c: Coincident(g5,g1)
    c: Parallel(g5,g4)
    c: Equal(g5,g4)
    c: Equal(g0,g3)
    c: DistanceX(g2,g2) = 75
    c: PointOnObject(g6,g4)
    c: Coincident(g10,g11)
    c: Coincident(g11,g12)
    c: Coincident(g12,g13)
    c: Coincident(g13,g10)
    c: Horizontal(g10)
    c: Horizontal(g12)
    c: Vertical(g11)
    c: Vertical(g13)
    c: Coincident(g10,g6)
    c: Coincident(g11,g8)
    c: Coincident(g7,g10)
    c: Coincident(g12,g9)
    c: Equal(g9,g8)
    c: Equal(g8,g7)
    c: Equal(g7,g6)
    c: Radius(g6) = 4
    c: DistanceX(g10,g10) = 56.5
    c: Equal(g13,g10)
    c: Symmetric(g7,g6,g-2)
    c: Coincident(g14,g-1)
    c: Radius(g14) = 10
FEATURE [PartDesign::Pad] Pad021
  BaseFeature = -> Pad020
  Length = 20
  Length2 = 100
  Placement = pos=(0,0,0) rot=(1,0,0;1.5708rad)
  Profile = -> Sketch027
  Refine = true
  Type = 0
  expr: Length = Medidas.gg - Medidas.bg
FEATURE [Sketcher::SketchObject] Sketch028
  ExternalGeometry = -> [Pad021]
  MapMode = 5
  Placement = pos=(0,-119.5,-1.23635e-11) rot=(1,0,0;1.5708rad)
  Support = -> [Pad021]
  expr: Constraints[114] = Medidas.rt * 1.25 + 4.5
  expr: Constraints[45] = Medidas.tg - 2.5 * Medidas.rt
  expr: Constraints[48] = Medidas.rt * 1.25
  sketch-geometry (37):
    g0: LineSegment StartX=-37.5 StartY=18.25 StartZ=0 EndX=-37.5 EndY=-18.25 EndZ=0
    g1: LineSegment StartX=-37.5 StartY=-18.25 StartZ=0 EndX=-28.25 EndY=-18.25 EndZ=0
    g2: LineSegment StartX=-18.25 StartY=-28.25 StartZ=0 EndX=-18.25 EndY=-37.5 EndZ=0
    g3: LineSegment StartX=-18.25 StartY=-37.5 StartZ=0 EndX=18.25 EndY=-37.5 EndZ=0
    g4: LineSegment StartX=18.25 StartY=-37.5 StartZ=0 EndX=18.25 EndY=-28.25 EndZ=0
    g5: LineSegment StartX=28.25 StartY=-18.25 StartZ=0 EndX=37.5 EndY=-18.25 EndZ=0
    g6: LineSegment StartX=37.5 StartY=-18.25 StartZ=0 EndX=37.5 EndY=18.25 EndZ=0
    g7: LineSegment StartX=37.5 StartY=18.25 StartZ=0 EndX=28.25 EndY=18.25 EndZ=0
    g8: LineSegment StartX=18.25 StartY=28.25 StartZ=0 EndX=18.25 EndY=37.5 EndZ=0
    g9: LineSegment StartX=18.25 StartY=37.5 StartZ=0 EndX=-18.25 EndY=37.5 EndZ=0
    g10: LineSegment StartX=-18.25 StartY=37.5 StartZ=0 EndX=-18.25 EndY=28.25 EndZ=0
    g11: LineSegment StartX=-28.25 StartY=18.25 StartZ=0 EndX=-37.5 EndY=18.25 EndZ=0
    g12: ArcOfCircle CenterX=-28.25 CenterY=28.25 CenterZ=0 NormalX=0 NormalY=0 NormalZ=1 AngleXU=0 Radius=10 StartAngle=4.71239 EndAngle=6.28319
    g13: ArcOfCircle CenterX=-28.25 CenterY=-28.25 CenterZ=0 NormalX=0 NormalY=0 NormalZ=1 AngleXU=0 Radius=10 StartAngle=0 EndAngle=1.5708
    g14: ArcOfCircle CenterX=28.25 CenterY=-28.25 CenterZ=0 NormalX=0 NormalY=0 NormalZ=1 AngleXU=0 Radius=10 StartAngle=1.5708 EndAngle=3.14159
    g15: ArcOfCircle CenterX=28.25 CenterY=28.25 CenterZ=0 NormalX=0 NormalY=0 NormalZ=1 AngleXU=0 Radius=10 StartAngle=3.14159 EndAngle=4.71239
    g16: LineSegment StartX=-13.75 StartY=33 StartZ=0 EndX=-13.75 EndY=28.25 EndZ=0
    g17: LineSegment StartX=-28.25 StartY=13.75 StartZ=0 EndX=-33 EndY=13.75 EndZ=0
    g18: LineSegment StartX=-33 StartY=13.75 StartZ=0 EndX=-33 EndY=-13.75 EndZ=0
    g19: LineSegment StartX=-33 StartY=-13.75 StartZ=0 EndX=-28.25 EndY=-13.75 EndZ=0
    g20: LineSegment StartX=-13.75 StartY=-28.25 StartZ=0 EndX=-13.75 EndY=-33 EndZ=0
    g21: LineSegment StartX=-13.75 StartY=-33 StartZ=0 EndX=13.75 EndY=-33 EndZ=0
    g22: LineSegment StartX=13.75 StartY=-33 StartZ=0 EndX=13.75 EndY=-28.25 EndZ=0
    g23: LineSegment StartX=28.25 StartY=-13.75 StartZ=0 EndX=33 EndY=-13.75 EndZ=0
    g24: LineSegment StartX=33 StartY=-13.75 StartZ=0 EndX=33 EndY=13.75 EndZ=0
    g25: LineSegment StartX=33 StartY=13.75 StartZ=0 EndX=28.25 EndY=13.75 EndZ=0
    g26: LineSegment StartX=13.75 StartY=28.25 StartZ=0 EndX=13.75 EndY=33 EndZ=0
    g27: LineSegment StartX=13.75 StartY=33 StartZ=0 EndX=-13.75 EndY=33 EndZ=0
    g28: LineSegment [constr] StartX=-33 StartY=-13.75 StartZ=0 EndX=-37.5 EndY=-13.75 EndZ=0
    g29: LineSegment [constr] StartX=33 StartY=-13.75 StartZ=0 EndX=37.5 EndY=-13.75 EndZ=0
    g30: LineSegment [constr] StartX=-13.75 StartY=33 StartZ=0 EndX=-13.75 EndY=37.5 EndZ=0
    g31: LineSegment [constr] StartX=-13.75 StartY=-33 StartZ=0 EndX=-13.75 EndY=-37.5 EndZ=0
    g32: LineSegment [constr] StartX=-33 StartY=-13.75 StartZ=0 EndX=-33 EndY=-18.25 EndZ=0
    g33: ArcOfCircle CenterX=-28.25 CenterY=28.25 CenterZ=0 NormalX=0 NormalY=0 NormalZ=1 AngleXU=0 Radius=14.5 StartAngle=4.71239 EndAngle=6.28319
    g34: ArcOfCircle CenterX=28.25 CenterY=28.25 CenterZ=0 NormalX=0 NormalY=0 NormalZ=1 AngleXU=0 Radius=14.5 StartAngle=3.14159 EndAngle=4.71239
    g35: ArcOfCircle CenterX=28.25 CenterY=-28.25 CenterZ=0 NormalX=0 NormalY=0 NormalZ=1 AngleXU=0 Radius=14.5 StartAngle=1.5708 EndAngle=3.14159
    g36: ArcOfCircle CenterX=-28.25 CenterY=-28.25 CenterZ=0 NormalX=0 NormalY=0 NormalZ=1 AngleXU=0 Radius=14.5 StartAngle=0 EndAngle=1.5708
  constraints (115):
    c: Coincident(g1,g0)
    c: Horizontal(g1)
    c: Vertical(g2)
    c: Coincident(g2,g3)
    c: Coincident(g3,g4)
    c: Vertical(g4)
    c: Horizontal(g5)
    c: Coincident(g5,g6)
    c: Coincident(g6,g7)
    c: Vertical(g8)
    c: Coincident(g8,g9)
    c: Horizontal(g9)
    c: Coincident(g9,g10)
    c: Coincident(g11,g0)
    c: Horizontal(g11)
    c: PointOnObject(g0,g-3)
    c: Symmetric(g0,g0,g-1)
    c: Symmetric(g6,g5,g-1)
    c: Symmetric(g8,g9,g-2)
    c: PointOnObject(g9,g-4)
    c: Vertical(g10)
    c: Horizontal(g7)
    c: Symmetric(g3,g2,g-2)
    c: PointOnObject(g3,g-6)
    c: Equal(g10,g8)
    c: Equal(g8,g7)
    c: Equal(g7,g5)
    c: Equal(g5,g4)
    c: Equal(g4,g2)
    c: Equal(g2,g1)
    c: Equal(g1,g11)
    c: Equal(g3,g0)
    c: Equal(g0,g9)
    c: Equal(g9,g6)
    c: Coincident(g12,g10)
    c: Coincident(g12,g11)
    c: Coincident(g13,g1)
    c: Coincident(g13,g2)
    c: Coincident(g14,g4)
    c: Coincident(g14,g5)
    c: Coincident(g15,g7)
    c: Coincident(g15,g8)
    c: Equal(g15,g12)
    c: Equal(g12,g13)
    c: Equal(g13,g14)
    c: DistanceX(g3,g3) = 36.5
    c: Vertical(g1,g13)
    c: PointOnObject(g6,g-5)
    c: Radius(g13) = 10
    c: Vertical(g16)
    c: Coincident(g17,g18)
    c: Vertical(g18)
    c: Coincident(g18,g19)
    c: Horizontal(g19)
    c: Vertical(g20)
    c: Coincident(g20,g21)
    c: Horizontal(g21)
    c: Coincident(g21,g22)
    c: Vertical(g22)
    c: Horizontal(g23)
    c: Coincident(g23,g24)
    c: Vertical(g24)
    c: Coincident(g24,g25)
    c: Horizontal(g25)
    c: Vertical(g26)
    c: Coincident(g26,g27)
    c: Coincident(g27,g16)
    c: Horizontal(g27)
    c: Symmetric(g26,g16,g-2)
    c: Symmetric(g17,g18,g-1)
    c: Symmetric(g20,g21,g-2)
    c: Symmetric(g23,g24,g-1)
    c: Equal(g24,g27)
    c: Equal(g27,g18)
    c: Equal(g18,g21)
    c: Equal(g20,g22)
    c: Equal(g22,g23)
    c: Equal(g23,g25)
    c: Equal(g25,g26)
    c: Equal(g26,g16)
    c: Equal(g16,g17)
    c: Equal(g17,g19)
    c: Horizontal(g17)
    c: Coincident(g18,g28)
    c: PointOnObject(g28,g0)
    c: Horizontal(g28)
    c: Coincident(g23,g29)
    c: PointOnObject(g29,g6)
    c: Horizontal(g29)
    c: Coincident(g16,g30)
    c: PointOnObject(g30,g9)
    c: Vertical(g30)
    c: Coincident(g20,g31)
    c: Vertical(g31)
    c: Equal(g29,g31)
    c: Equal(g31,g28)
    c: Equal(g28,g30)
    c: DistanceX(g28,g28) = 4.5
    c: Vertical(g32)
    c: PointOnObject(g32,g1)
    c: Coincident(g18,g32)
    c: Equal(g32,g28)
    c: PointOnObject(g31,g3)
    c: Coincident(g33,g16)
    c: Coincident(g33,g17)
    c: Coincident(g34,g25)
    c: Coincident(g34,g26)
    c: Coincident(g35,g22)
    c: Coincident(g35,g23)
    c: Tangent(g36,g19) = 1.5708
    c: Tangent(g36,g20) = 1.5708
    c: Vertical(g35,g23)
    c: Equal(g33,g34)
    c: Equal(g34,g35)
    c: Radius(g35) = 14.5
FEATURE [PartDesign::Pad] Pad022
  BaseFeature = -> Pad021
  Length = 16
  Length2 = 100
  Placement = pos=(0,0,0) rot=(1,0,0;1.5708rad)
  Profile = -> Sketch028
  Refine = true
  Type = 0
  expr: Length = Medidas.bg
FEATURE [Sketcher::SketchObject] Sketch029
  MapMode = 5
  Placement = pos=(0,-119.5,-1.23635e-11) rot=(1,0,0;1.5708rad)
  Support = -> [Pad022]
  expr: Constraints[3] = Medidas.b / 2 * 1.1
  expr: Constraints[2] = Medidas.mmm / 2
  sketch-geometry (2):
    g0: Circle CenterX=0 CenterY=0 CenterZ=0 NormalX=0 NormalY=0 NormalZ=1 AngleXU=0 Radius=10
    g1: Circle CenterX=0 CenterY=0 CenterZ=0 NormalX=0 NormalY=0 NormalZ=1 AngleXU=0 Radius=24.75
  constraints (4):
    c: Coincident(g0,g-1)
    c: Coincident(g1,g-1)
    c: Radius(g0) = 10
    c: Radius(g1) = 24.75
FEATURE [PartDesign::Pad] Pad023
  BaseFeature = -> Pad022
  Length = 22
  Length2 = 100
  Placement = pos=(0,0,0) rot=(1,0,0;1.5708rad)
  Profile = -> Sketch029
  Refine = true
  Type = 0
  expr: Length = Medidas.bg + Medidas.vd
FEATURE [Sketcher::SketchObject] Sketch030
  MapMode = 5
  Placement = pos=(0,-134,-1.3893e-11) rot=(1,0,0;1.5708rad)
  Support = -> [Pad023]
  expr: Constraints[3] = Medidas.mmm / 2
  expr: Constraints[2] = Medidas.b / 2
  sketch-geometry (2):
    g0: Circle CenterX=0 CenterY=0 CenterZ=0 NormalX=0 NormalY=0 NormalZ=1 AngleXU=0 Radius=20
    g1: Circle CenterX=0 CenterY=0 CenterZ=0 NormalX=0 NormalY=0 NormalZ=1 AngleXU=0 Radius=10
  constraints (4):
    c: Coincident(g0,g-1)
    c: Coincident(g1,g-1)
    c: Radius(g0) = 22.5
    c: Radius(g1) = 10
FEATURE [PartDesign::Pad] Pad024
  BaseFeature = -> Pad023
  Length = 20.5
  Length2 = 100
  Placement = pos=(0,0,0) rot=(1,0,0;1.5708rad)
  Profile = -> Sketch030
  Refine = true
  Type = 0
  expr: Length = Medidas.l2 - Medidas.vd
FEATURE [PartDesign::Mirrored] Mirrored004
  BaseFeature = -> Pad024
  MirrorPlane = -> XZ_Plane009
  Originals = -> [Pad021]
  Placement = pos=(0,0,0) rot=(1,0,0;1.5708rad)
  Refine = true
FEATURE [PartDesign::Mirrored] Mirrored005
  BaseFeature = -> Mirrored004
  MirrorPlane = -> XZ_Plane009
  Originals = -> [Pad022]
  Placement = pos=(0,0,0) rot=(1,0,0;1.5708rad)
  Refine = true
FEATURE [Sketcher::SketchObject] Sketch031
  MapMode = 5
  Placement = pos=(0,0,0) rot=(1,0,0;1.5708rad)
  Support = -> [XZ_Plane010]
  expr: Constraints[1] = Medidas.b / 2 * 0.95
  sketch-geometry (1):
    g0: Circle CenterX=0 CenterY=0 CenterZ=0 NormalX=0 NormalY=0 NormalZ=1 AngleXU=0 Radius=21.375
  constraints (2):
    c: Coincident(g0,g-1)
    c: Radius(g0) = 21.375
FEATURE [PartDesign::Pad] Pad025
  Length = 10
  Length2 = 100
  Placement = pos=(0,0,0) rot=(1,0,0;1.5708rad)
  Profile = -> Sketch031
  Refine = true
  Type = 0
FEATURE [Sketcher::SketchObject] Sketch032
  MapMode = 5
  Placement = pos=(0,0,0) rot=(-1,0,0;1.5708rad)
  Support = -> [Pad025]
  expr: Constraints[1] = Medidas.mmm / 2
  sketch-geometry (1):
    g0: Circle CenterX=0 CenterY=0 CenterZ=0 NormalX=0 NormalY=0 NormalZ=1 AngleXU=0 Radius=10
  constraints (2):
    c: Coincident(g0,g-1)
    c: Radius(g0) = 10
FEATURE [PartDesign::Pad] Pad026
  BaseFeature = -> Pad025
  Length = 271
  Length2 = 100
  Placement = pos=(0,0,0) rot=(1,0,0;1.5708rad)
  Profile = -> Sketch032
  Refine = true
  Reversed = true
  Type = 0
  expr: Length = Medidas.l8 + Medidas.carrera
FEATURE [Sketcher::SketchObject] Sketch033
  MapMode = 5
  Placement = pos=(0,-271,-2.80404e-11) rot=(1,0,0;1.5708rad)
  Support = -> [Pad026]
  expr: Constraints[22] = Medidas.sw
  expr: Constraints[19] = Medidas.sw
  sketch-geometry (8):
    g0: LineSegment StartX=-25.5 StartY=8.5 StartZ=0 EndX=-8.5 EndY=8.5 EndZ=0
    g1: LineSegment StartX=-8.5 StartY=8.5 StartZ=0 EndX=-8.5 EndY=-8.5 EndZ=0
    g2: LineSegment StartX=-8.5 StartY=-8.5 StartZ=0 EndX=-25.5 EndY=-8.5 EndZ=0
    g3: LineSegment StartX=-25.5 StartY=-8.5 StartZ=0 EndX=-25.5 EndY=8.5 EndZ=0
    g4: LineSegment StartX=25.5 StartY=8.5 StartZ=0 EndX=8.5 EndY=8.5 EndZ=0
    g5: LineSegment StartX=8.5 StartY=8.5 StartZ=0 EndX=8.5 EndY=-8.5 EndZ=0
    g6: LineSegment StartX=8.5 StartY=-8.5 StartZ=0 EndX=25.5 EndY=-8.5 EndZ=0
    g7: LineSegment StartX=25.5 StartY=-8.5 StartZ=0 EndX=25.5 EndY=8.5 EndZ=0
  constraints (23):
    c: Coincident(g0,g1)
    c: Coincident(g1,g2)
    c: Coincident(g2,g3)
    c: Coincident(g3,g0)
    c: Horizontal(g0)
    c: Horizontal(g2)
    c: Vertical(g1)
    c: Vertical(g3)
    c: Coincident(g4,g5)
    c: Coincident(g5,g6)
    c: Coincident(g6,g7)
    c: Coincident(g7,g4)
    c: Horizontal(g4)
    c: Horizontal(g6)
    c: Vertical(g5)
    c: Vertical(g7)
    c: Symmetric(g0,g4,g-2)
    c: Equal(g5,g1)
    c: Equal(g6,g2)
    c: DistanceX(g0,g4) = 17
    c: Symmetric(g0,g2,g-1)
    c: Equal(g0,g3)
    c: DistanceX(g0,g0) = 17
FEATURE [PartDesign::Pocket] Pocket004
  BaseFeature = -> Pad026
  Length = 8
  Length2 = 100
  Placement = pos=(0,0,0) rot=(1,0,0;1.5708rad)
  Profile = -> Sketch033
  Refine = true
  Type = 0
  expr: Length = Medidas.kw
FEATURE [Sketcher::SketchObject] Sketch034
  MapMode = 5
  Placement = pos=(0,-271,-2.80404e-11) rot=(1,0,0;1.5708rad)
  Support = -> [Pocket004]
  expr: Constraints[1] = Medidas.kk / 2
  sketch-geometry (1):
    g0: Circle CenterX=0 CenterY=0 CenterZ=0 NormalX=0 NormalY=0 NormalZ=1 AngleXU=0 Radius=8
  constraints (2):
    c: Coincident(g0,g-1)
    c: Radius(g0) = 8
FEATURE [Part::Helix] Helix002  label="Thread Helice002"
  Angle = 0
  AttacherType = Attacher::AttachEngine3D
  Height = 32
  LocalCoord = 0
  Pitch = 1.5
  Placement = pos=(0,0,0) rot=(-1,0,0;1.5708rad)
  Radius = 8
  Style = 1
  expr: Radius = Medidas.kk / 2
  expr: Height = Medidas.am
  expr: Pitch = Medidas.kkp
FEATURE [App::MeasureDistance] Distance001  label="WH001"
  Distance = 36
  P1 = (0,-171.5,0)
  P2 = (0,-135.5,0)
  expr: P2.y = -(Medidas.l8 + Medidas.carrera) / 2
FEATURE [Sketcher::SketchObject] Sketch035
  MapMode = 5
  Support = -> [XY_Plane011]
  expr: Constraints[6] = Medidas.kk / 2 * 0.96
  sketch-geometry (3):
    g0: LineSegment StartX=7.68 StartY=0.4 StartZ=0 EndX=7.68 EndY=-0.4 EndZ=0
    g1: LineSegment StartX=7.68 StartY=-0.4 StartZ=0 EndX=8.68 EndY=0 EndZ=0
    g2: LineSegment StartX=8.68 StartY=0 StartZ=0 EndX=7.68 EndY=0.4 EndZ=0
  constraints (9):
    c: Vertical(g0)
    c: Coincident(g0,g1)
    c: PointOnObject(g1,g-1)
    c: Coincident(g1,g2)
    c: Coincident(g2,g0)
    c: Symmetric(g0,g0,g-1)
    c: DistanceX(g-1,g0) = 7.68
    c: DistanceX(g0,g1) = 1
    c: DistanceY(g0,g0) = 0.8
FEATURE [PartDesign::ShapeBinder] ReferenceHelix003  label="ReferenceHelix002"
  Placement = pos=(0,0,0) rot=(-1,0,0;1.5708rad)
  Support = -> [Helix002]
  TraceSupport = false
FEATURE [PartDesign::AdditivePipe] AdditivePipe002
  AuxilleryCurvelinear = true
  AuxillerySpineTangent = false
  Binormal = (0,0,0)
  Mode = 2
  Profile = -> Sketch035
  Refine = true
  Spine = -> ReferenceHelix003 [Edge1,Edge2,Edge3,Edge4,Edge5,Edge6,Edge7,Edge8,Edge9,Edge10,Edge11,Edge12,Edge13,Edge14,Edge15,Edge16,Edge17,Edge18,Edge19,Edge20]
  SpineTangent = false
  Transformation = 0
  Transition = 0
FEATURE [PartDesign::Body] Body008  label="Thread002"
  Group = -> [Sketch035,AdditivePipe002,ReferenceHelix003]
  Origin = -> Origin011
  Placement = pos=(0,-300.5,0) rot=(0,0,1;0rad)
  Tip = -> AdditivePipe002
  expr: Placement.Base.y = -Medidas.l8 - Medidas.carrera - Medidas.l2 - 3
FEATURE [PartDesign::Pad] Pad027
  BaseFeature = -> Pocket004
  Length = 32
  Length2 = 100
  Placement = pos=(0,0,0) rot=(1,0,0;1.5708rad)
  Profile = -> Sketch034
  Refine = true
  Type = 0
  expr: Length = Medidas.am
FEATURE [PartDesign::Body] Body007  label="Piston+rod002"
  Group = -> [Sketch031,Pad025,Sketch032,Pad026,Sketch033,Pocket004,Sketch034,Pad027]
  Origin = -> Origin010
  Tip = -> Pad027
FEATURE [Part::Fuse] Fusion002  label="Piston Rod002"
  Base = -> Body007
  Placement = pos=(0,94.5,0) rot=(0,0,1;0rad)
  Refine = true
  Tool = -> Body008
  expr: Placement.Base.y = (Medidas.l8 + Medidas.carrera) / 2 - Medidas.gg + -Medidas.delta
FEATURE [Sketcher::SketchObject] Sketch036
  MapMode = 5
  Placement = pos=(0,119.5,1.23671e-11) rot=(-1,0,0;1.5708rad)
  Support = -> [Mirrored005]
  expr: Constraints[1] = Medidas.b / 2
  sketch-geometry (1):
    g0: Circle CenterX=0 CenterY=0 CenterZ=0 NormalX=0 NormalY=0 NormalZ=1 AngleXU=0 Radius=22.5
  constraints (2):
    c: Coincident(g0,g-1)
    c: Radius(g0) = 22.5
FEATURE [PartDesign::Pad] Pad028
  BaseFeature = -> Mirrored005
  Length = 20
  Length2 = 100
  Placement = pos=(0,0,0) rot=(1,0,0;1.5708rad)
  Profile = -> Sketch036
  Refine = true
  Type = 0
  expr: Length = Medidas.bg + Medidas.va
FEATURE [PartDesign::Fillet] Fillet002
  Base = -> Pad028 [Edge28,Edge39,Edge21,Edge27,Edge174,Edge173,Edge180,Edge186]
  BaseFeature = -> Pad028
  Placement = pos=(0,0,0) rot=(1,0,0;1.5708rad)
  Radius = 4
  expr: Radius = Medidas.rt / 2
FEATURE [PartDesign::Chamfer] Chamfer002
  Base = -> Fillet002 [Edge307]
  BaseFeature = -> Fillet002
  Placement = pos=(0,0,0) rot=(1,0,0;1.5708rad)
  Size = 2
  expr: Size = Medidas.va / 2
FEATURE [Sketcher::SketchObject] Sketch037
  MapMode = 5
  Placement = pos=(0,-3.8693e-12,37.5) rot=(0,0,1;3.14159rad)
  Support = -> [Chamfer002]
  expr: Constraints[5] = Medidas.l8 + Medidas.carrera - 2 * Medidas.pl
  expr: Constraints[3] = Medidas.eee / 2
  sketch-geometry (2):
    g0: Circle CenterX=0 CenterY=121.5 CenterZ=0 NormalX=0 NormalY=0 NormalZ=1 AngleXU=0 Radius=7.5
    g1: Circle CenterX=0 CenterY=-121.5 CenterZ=0 NormalX=0 NormalY=0 NormalZ=1 AngleXU=0 Radius=7.5
  constraints (6):
    c: PointOnObject(g0,g-2)
    c: PointOnObject(g1,g-2)
    c: Equal(g1,g0)
    c: Radius(g0) = 7.5
    c: Symmetric(g0,g1,g-1)
    c: DistanceY(g1,g0) = 243
FEATURE [PartDesign::Pocket] Pocket005
  BaseFeature = -> Chamfer002
  Length = 22.5
  Length2 = 100
  Placement = pos=(0,0,0) rot=(1,0,0;1.5708rad)
  Profile = -> Sketch037
  Refine = true
  Type = 0
  expr: Length = Medidas.b / 2
FEATURE [Sketcher::SketchObject] Sketch038
  MapMode = 5
  Placement = pos=(0,-3.8693e-12,37.5) rot=(0,0,1;3.14159rad)
  Support = -> [Pocket005]
  expr: Constraints[9] = Medidas.l8 + Medidas.carrera - 2 * Medidas.pl
  expr: Constraints[5] = Medidas.eee * 7 / 8
  expr: Constraints[4] = Medidas.eee / 2
  sketch-geometry (4):
    g0: Circle CenterX=0 CenterY=121.5 CenterZ=0 NormalX=0 NormalY=0 NormalZ=1 AngleXU=0 Radius=13.125
    g1: Circle CenterX=0 CenterY=121.5 CenterZ=0 NormalX=0 NormalY=0 NormalZ=1 AngleXU=0 Radius=7.5
    g2: Circle CenterX=0 CenterY=-121.5 CenterZ=0 NormalX=0 NormalY=0 NormalZ=1 AngleXU=0 Radius=13.125
    g3: Circle CenterX=0 CenterY=-121.5 CenterZ=0 NormalX=0 NormalY=0 NormalZ=1 AngleXU=0 Radius=7.5
  constraints (10):
    c: PointOnObject(g0,g-2)
    c: Coincident(g1,g0)
    c: PointOnObject(g2,g-2)
    c: Coincident(g3,g2)
    c: Radius(g3) = 7.5
    c: Radius(g2) = 13.125
    c: Equal(g3,g1)
    c: Equal(g0,g2)
    c: Symmetric(g2,g0,g-1)
    c: DistanceY(g2,g0) = 243
FEATURE [PartDesign::Pad] Pad029
  BaseFeature = -> Pocket005
  Length = 22.5
  Length2 = 100
  Placement = pos=(0,0,0) rot=(1,0,0;1.5708rad)
  Profile = -> Sketch038
  Refine = true
  Reversed = true
  Type = 0
  expr: Length = Medidas.b / 2
FEATURE [PartDesign::Body] Body006  label="Barrel+Endcap002"
  Group = -> [Sketch026,Pad020,Sketch027,Pad021,Sketch028,Pad022,Sketch029,Pad023,Sketch030,Pad024,Mirrored004,Mirrored005,Sketch036,Pad028,Fillet002,Chamfer002,Sketch037,Pocket005,Sketch038,Pad029]
  Origin = -> Origin009
  Tip = -> Pad029
FEATURE [App::Part] Part002
  Group = -> [Body006,Body007,Helix002,Body008,Fusion002]
  Id = DA-XX-XXX-TCA
  License = CC BY 3.0
  LicenseURL = http://creativecommons.org/licenses/by/3.0/
  Origin = -> Origin008
  Placement = pos=(209.5,0,0) rot=(0,0,1;0rad)
  Type = Pneumatic cylinder
